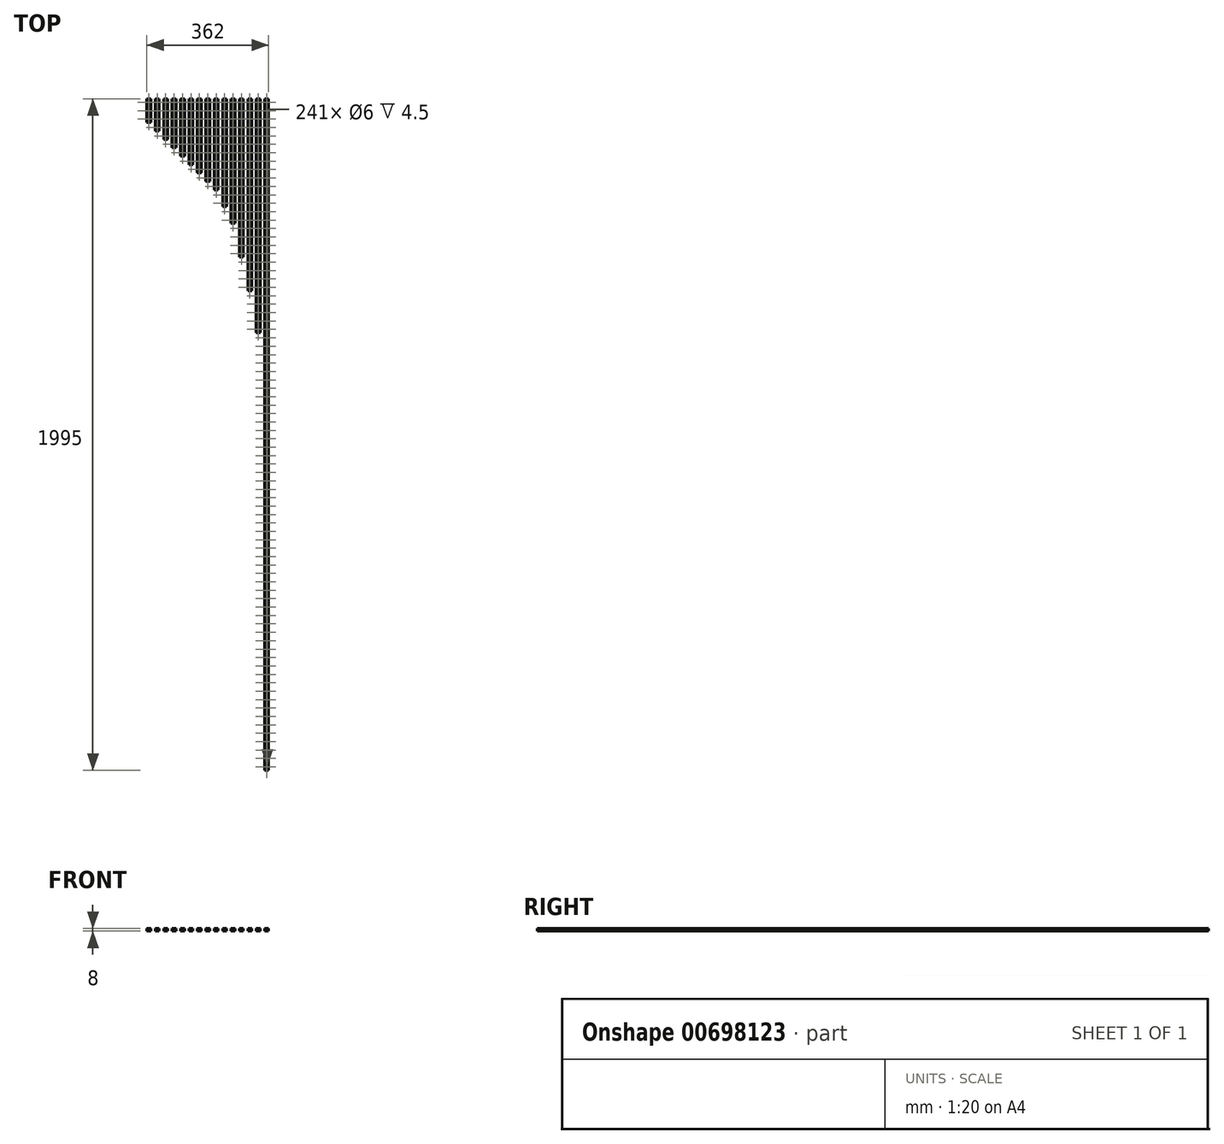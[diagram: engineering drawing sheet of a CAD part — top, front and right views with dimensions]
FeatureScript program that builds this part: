
annotation { "Feature Type Name" : "Feature", "Feature Type Description" : "" }
export const myFeature = defineFeature(function(context is Context, id is Id, definition is map)
    precondition{}
    {
        {
            var Q0;
            Q0=qCreatedBy(makeId("Front.planeOp"),FACE);
            var sketch = newSketch(context, id + "F0", { "sketchPlane" : qUnion([Q0])});
            skPoint(sketch, "E0.middle", {"position": v(0, 0) * mm});
            skLineSegment(sketch, "E1.bottom", {"start": v(5.5, -4) * mm, "end": v(-5.5, -4) * mm});
            skLineSegment(sketch, "E1.top", {"start": v(5.5, 4) * mm, "end": v(-5.5, 4) * mm});
            skLineSegment(sketch, "E1.left", {"start": v(6, -3.5) * mm, "end": v(6, -0.03) * mm});
            skLineSegment(sketch, "E1.right", {"start": v(-6, -3.5) * mm, "end": v(-6, -0.03) * mm});
            skArc(sketch, "E2", {"start": v(-6, -0.03) * mm, "mid": v(-5.5, 0.27) * mm, "end": v(-5.15, 0.75) * mm});
            skArc(sketch, "E3", {"start": v(6, 2.63) * mm, "mid": v(5.5, 2.33) * mm, "end": v(5.15, 1.85) * mm});
            skLineSegment(sketch, "E4", {"start": v(4.45, 1.85) * mm, "end": v(5.15, 1.85) * mm});
            skLineSegment(sketch, "E5", {"start": v(4.45, 0.75) * mm, "end": v(5.15, 0.75) * mm});
            skLineSegment(sketch, "E6", {"start": v(-4.45, 0.75) * mm, "end": v(-5.15, 0.75) * mm});
            skLineSegment(sketch, "E7", {"start": v(-4.45, 1.85) * mm, "end": v(-5.15, 1.85) * mm});
            skLineSegment(sketch, "E8", {"start": v(-6, 3.5) * mm, "end": v(-5.5, 4) * mm});
            skLineSegment(sketch, "E9.MirrorCS", {"start": v(6, 3.5) * mm, "end": v(5.5, 4) * mm});
            skLineSegment(sketch, "E10.MirrorCS", {"start": v(6, -3.5) * mm, "end": v(5.5, -4) * mm});
            skLineSegment(sketch, "E11.MirrorCS", {"start": v(-6, -3.5) * mm, "end": v(-5.5, -4) * mm});
            skPoint(sketch, "E12.orphan", {"position": v(-6, 4) * mm});
            skLineSegment(sketch, "E13.trimOffspring", {"start": v(-6, 2.63) * mm, "end": v(-6, 3.5) * mm});
            skArc(sketch, "E14.trimOffspring", {"start": v(-5.15, 1.85) * mm, "mid": v(-5.5, 2.33) * mm, "end": v(-6, 2.63) * mm});
            skPoint(sketch, "E15.orphan", {"position": v(6, 4) * mm});
            skLineSegment(sketch, "E16.trimOffspring", {"start": v(6, 2.63) * mm, "end": v(6, 3.5) * mm});
            skArc(sketch, "E17.trimOffspring", {"start": v(5.15, 0.75) * mm, "mid": v(5.5, 0.27) * mm, "end": v(6, -0.03) * mm});
            skPoint(sketch, "E18.orphan", {"position": v(6, -4) * mm});
            skPoint(sketch, "E19.orphan", {"position": v(-6, -4) * mm});
            skLineSegment(sketch, "E20", {"start": v(-4.45, 1.85) * mm, "end": v(-4.45, 0.75) * mm});
            skLineSegment(sketch, "E21", {"start": v(4.45, 1.85) * mm, "end": v(4.45, 0.75) * mm});
            skLineSegment(sketch, "E22", {"start": v(-6.44, 1.3) * mm, "end": v(6.44, 1.3) * mm, "construction": true});
            skLineSegment(sketch, "E23.1.0.0", {"start": v(18.56, 1.3) * mm, "end": v(31.44, 1.3) * mm, "construction": true});
            skLineSegment(sketch, "E23.1.0.1", {"start": v(19, -3.5) * mm, "end": v(19, -0.03) * mm});
            skLineSegment(sketch, "E23.1.0.2", {"start": v(31, -3.5) * mm, "end": v(31, -0.03) * mm});
            skLineSegment(sketch, "E23.1.0.3", {"start": v(30.5, -4) * mm, "end": v(19.5, -4) * mm});
            skLineSegment(sketch, "E23.1.0.4", {"start": v(30.5, 4) * mm, "end": v(19.5, 4) * mm});
            skPoint(sketch, "E23.1.0.5", {"position": v(25, 0) * mm});
            skPoint(sketch, "E23.1.0.6", {"position": v(19, -4) * mm});
            skPoint(sketch, "E23.1.0.7", {"position": v(19, 4) * mm});
            skPoint(sketch, "E23.1.0.8", {"position": v(31, 4) * mm});
            skPoint(sketch, "E23.1.0.9", {"position": v(31, -4) * mm});
            skPoint(sketch, "E23.1.0.10", {"position": v(25, 0) * mm});
            skLineSegment(sketch, "E23.1.0.11", {"start": v(31, -3.5) * mm, "end": v(30.5, -4) * mm});
            skLineSegment(sketch, "E23.1.0.12", {"start": v(31, 3.5) * mm, "end": v(30.5, 4) * mm});
            skLineSegment(sketch, "E23.1.0.13", {"start": v(19, -3.5) * mm, "end": v(19.5, -4) * mm});
            skLineSegment(sketch, "E23.1.0.14", {"start": v(20.55, 1.85) * mm, "end": v(19.85, 1.85) * mm});
            skLineSegment(sketch, "E23.1.0.15", {"start": v(19, 2.63) * mm, "end": v(19, 3.5) * mm});
            skLineSegment(sketch, "E23.1.0.16", {"start": v(31, 2.63) * mm, "end": v(31, 3.5) * mm});
            skArc(sketch, "E23.1.0.17", {"start": v(30.15, 0.75) * mm, "mid": v(30.5, 0.27) * mm, "end": v(31, -0.03) * mm});
            skLineSegment(sketch, "E23.1.0.18", {"start": v(20.55, 1.85) * mm, "end": v(20.55, 0.75) * mm});
            skLineSegment(sketch, "E23.1.0.19", {"start": v(29.45, 0.75) * mm, "end": v(30.15, 0.75) * mm});
            skLineSegment(sketch, "E23.1.0.20", {"start": v(20.55, 0.75) * mm, "end": v(19.85, 0.75) * mm});
            skArc(sketch, "E23.1.0.21", {"start": v(19, -0.03) * mm, "mid": v(19.5, 0.27) * mm, "end": v(19.85, 0.75) * mm});
            skLineSegment(sketch, "E23.1.0.22", {"start": v(19, 3.5) * mm, "end": v(19.5, 4) * mm});
            skArc(sketch, "E23.1.0.23", {"start": v(19.85, 1.85) * mm, "mid": v(19.5, 2.33) * mm, "end": v(19, 2.63) * mm});
            skLineSegment(sketch, "E23.1.0.24", {"start": v(29.45, 1.85) * mm, "end": v(30.15, 1.85) * mm});
            skArc(sketch, "E23.1.0.25", {"start": v(31, 2.63) * mm, "mid": v(30.5, 2.33) * mm, "end": v(30.15, 1.85) * mm});
            skArc(sketch, "E23.1.0.26", {"start": v(30.15, 0.75) * mm, "mid": v(30.5, 0.27) * mm, "end": v(31, -0.03) * mm});
            skLineSegment(sketch, "E23.1.0.27", {"start": v(29.45, 1.85) * mm, "end": v(29.45, 0.75) * mm});
            skLineSegment(sketch, "E23.2.0.0", {"start": v(43.56, 1.3) * mm, "end": v(56.44, 1.3) * mm, "construction": true});
            skLineSegment(sketch, "E23.2.0.1", {"start": v(44, -3.5) * mm, "end": v(44, -0.03) * mm});
            skLineSegment(sketch, "E23.2.0.2", {"start": v(56, -3.5) * mm, "end": v(56, -0.03) * mm});
            skLineSegment(sketch, "E23.2.0.3", {"start": v(55.5, -4) * mm, "end": v(44.5, -4) * mm});
            skLineSegment(sketch, "E23.2.0.4", {"start": v(55.5, 4) * mm, "end": v(44.5, 4) * mm});
            skPoint(sketch, "E23.2.0.5", {"position": v(50, 0) * mm});
            skPoint(sketch, "E23.2.0.6", {"position": v(44, -4) * mm});
            skPoint(sketch, "E23.2.0.7", {"position": v(44, 4) * mm});
            skPoint(sketch, "E23.2.0.8", {"position": v(56, 4) * mm});
            skPoint(sketch, "E23.2.0.9", {"position": v(56, -4) * mm});
            skPoint(sketch, "E23.2.0.10", {"position": v(50, 0) * mm});
            skLineSegment(sketch, "E23.2.0.11", {"start": v(56, -3.5) * mm, "end": v(55.5, -4) * mm});
            skLineSegment(sketch, "E23.2.0.12", {"start": v(56, 3.5) * mm, "end": v(55.5, 4) * mm});
            skLineSegment(sketch, "E23.2.0.13", {"start": v(44, -3.5) * mm, "end": v(44.5, -4) * mm});
            skLineSegment(sketch, "E23.2.0.14", {"start": v(45.55, 1.85) * mm, "end": v(44.85, 1.85) * mm});
            skLineSegment(sketch, "E23.2.0.15", {"start": v(44, 2.63) * mm, "end": v(44, 3.5) * mm});
            skLineSegment(sketch, "E23.2.0.16", {"start": v(56, 2.63) * mm, "end": v(56, 3.5) * mm});
            skArc(sketch, "E23.2.0.17", {"start": v(55.15, 0.75) * mm, "mid": v(55.5, 0.27) * mm, "end": v(56, -0.03) * mm});
            skLineSegment(sketch, "E23.2.0.18", {"start": v(45.55, 1.85) * mm, "end": v(45.55, 0.75) * mm});
            skLineSegment(sketch, "E23.2.0.19", {"start": v(54.45, 0.75) * mm, "end": v(55.15, 0.75) * mm});
            skLineSegment(sketch, "E23.2.0.20", {"start": v(45.55, 0.75) * mm, "end": v(44.85, 0.75) * mm});
            skArc(sketch, "E23.2.0.21", {"start": v(44, -0.03) * mm, "mid": v(44.5, 0.27) * mm, "end": v(44.85, 0.75) * mm});
            skLineSegment(sketch, "E23.2.0.22", {"start": v(44, 3.5) * mm, "end": v(44.5, 4) * mm});
            skArc(sketch, "E23.2.0.23", {"start": v(44.85, 1.85) * mm, "mid": v(44.5, 2.33) * mm, "end": v(44, 2.63) * mm});
            skLineSegment(sketch, "E23.2.0.24", {"start": v(54.45, 1.85) * mm, "end": v(55.15, 1.85) * mm});
            skArc(sketch, "E23.2.0.25", {"start": v(56, 2.63) * mm, "mid": v(55.5, 2.33) * mm, "end": v(55.15, 1.85) * mm});
            skArc(sketch, "E23.2.0.26", {"start": v(55.15, 0.75) * mm, "mid": v(55.5, 0.27) * mm, "end": v(56, -0.03) * mm});
            skLineSegment(sketch, "E23.2.0.27", {"start": v(54.45, 1.85) * mm, "end": v(54.45, 0.75) * mm});
            skLineSegment(sketch, "E23.3.0.0", {"start": v(68.56, 1.3) * mm, "end": v(81.44, 1.3) * mm, "construction": true});
            skLineSegment(sketch, "E23.3.0.1", {"start": v(69, -3.5) * mm, "end": v(69, -0.03) * mm});
            skLineSegment(sketch, "E23.3.0.2", {"start": v(81, -3.5) * mm, "end": v(81, -0.03) * mm});
            skLineSegment(sketch, "E23.3.0.3", {"start": v(80.5, -4) * mm, "end": v(69.5, -4) * mm});
            skLineSegment(sketch, "E23.3.0.4", {"start": v(80.5, 4) * mm, "end": v(69.5, 4) * mm});
            skPoint(sketch, "E23.3.0.5", {"position": v(75, 0) * mm});
            skPoint(sketch, "E23.3.0.6", {"position": v(69, -4) * mm});
            skPoint(sketch, "E23.3.0.7", {"position": v(69, 4) * mm});
            skPoint(sketch, "E23.3.0.8", {"position": v(81, 4) * mm});
            skPoint(sketch, "E23.3.0.9", {"position": v(81, -4) * mm});
            skPoint(sketch, "E23.3.0.10", {"position": v(75, 0) * mm});
            skLineSegment(sketch, "E23.3.0.11", {"start": v(81, -3.5) * mm, "end": v(80.5, -4) * mm});
            skLineSegment(sketch, "E23.3.0.12", {"start": v(81, 3.5) * mm, "end": v(80.5, 4) * mm});
            skLineSegment(sketch, "E23.3.0.13", {"start": v(69, -3.5) * mm, "end": v(69.5, -4) * mm});
            skLineSegment(sketch, "E23.3.0.14", {"start": v(70.55, 1.85) * mm, "end": v(69.85, 1.85) * mm});
            skLineSegment(sketch, "E23.3.0.15", {"start": v(69, 2.63) * mm, "end": v(69, 3.5) * mm});
            skLineSegment(sketch, "E23.3.0.16", {"start": v(81, 2.63) * mm, "end": v(81, 3.5) * mm});
            skArc(sketch, "E23.3.0.17", {"start": v(80.15, 0.75) * mm, "mid": v(80.5, 0.27) * mm, "end": v(81, -0.03) * mm});
            skLineSegment(sketch, "E23.3.0.18", {"start": v(70.55, 1.85) * mm, "end": v(70.55, 0.75) * mm});
            skLineSegment(sketch, "E23.3.0.19", {"start": v(79.45, 0.75) * mm, "end": v(80.15, 0.75) * mm});
            skLineSegment(sketch, "E23.3.0.20", {"start": v(70.55, 0.75) * mm, "end": v(69.85, 0.75) * mm});
            skArc(sketch, "E23.3.0.21", {"start": v(69, -0.03) * mm, "mid": v(69.5, 0.27) * mm, "end": v(69.85, 0.75) * mm});
            skLineSegment(sketch, "E23.3.0.22", {"start": v(69, 3.5) * mm, "end": v(69.5, 4) * mm});
            skArc(sketch, "E23.3.0.23", {"start": v(69.85, 1.85) * mm, "mid": v(69.5, 2.33) * mm, "end": v(69, 2.63) * mm});
            skLineSegment(sketch, "E23.3.0.24", {"start": v(79.45, 1.85) * mm, "end": v(80.15, 1.85) * mm});
            skArc(sketch, "E23.3.0.25", {"start": v(81, 2.63) * mm, "mid": v(80.5, 2.33) * mm, "end": v(80.15, 1.85) * mm});
            skArc(sketch, "E23.3.0.26", {"start": v(80.15, 0.75) * mm, "mid": v(80.5, 0.27) * mm, "end": v(81, -0.03) * mm});
            skLineSegment(sketch, "E23.3.0.27", {"start": v(79.45, 1.85) * mm, "end": v(79.45, 0.75) * mm});
            skLineSegment(sketch, "E23.4.0.0", {"start": v(93.56, 1.3) * mm, "end": v(106.44, 1.3) * mm, "construction": true});
            skLineSegment(sketch, "E23.4.0.1", {"start": v(94, -3.5) * mm, "end": v(94, -0.03) * mm});
            skLineSegment(sketch, "E23.4.0.2", {"start": v(106, -3.5) * mm, "end": v(106, -0.03) * mm});
            skLineSegment(sketch, "E23.4.0.3", {"start": v(105.5, -4) * mm, "end": v(94.5, -4) * mm});
            skLineSegment(sketch, "E23.4.0.4", {"start": v(105.5, 4) * mm, "end": v(94.5, 4) * mm});
            skPoint(sketch, "E23.4.0.5", {"position": v(100, 0) * mm});
            skPoint(sketch, "E23.4.0.6", {"position": v(94, -4) * mm});
            skPoint(sketch, "E23.4.0.7", {"position": v(94, 4) * mm});
            skPoint(sketch, "E23.4.0.8", {"position": v(106, 4) * mm});
            skPoint(sketch, "E23.4.0.9", {"position": v(106, -4) * mm});
            skPoint(sketch, "E23.4.0.10", {"position": v(100, 0) * mm});
            skLineSegment(sketch, "E23.4.0.11", {"start": v(106, -3.5) * mm, "end": v(105.5, -4) * mm});
            skLineSegment(sketch, "E23.4.0.12", {"start": v(106, 3.5) * mm, "end": v(105.5, 4) * mm});
            skLineSegment(sketch, "E23.4.0.13", {"start": v(94, -3.5) * mm, "end": v(94.5, -4) * mm});
            skLineSegment(sketch, "E23.4.0.14", {"start": v(95.55, 1.85) * mm, "end": v(94.85, 1.85) * mm});
            skLineSegment(sketch, "E23.4.0.15", {"start": v(94, 2.63) * mm, "end": v(94, 3.5) * mm});
            skLineSegment(sketch, "E23.4.0.16", {"start": v(106, 2.63) * mm, "end": v(106, 3.5) * mm});
            skArc(sketch, "E23.4.0.17", {"start": v(105.15, 0.75) * mm, "mid": v(105.5, 0.27) * mm, "end": v(106, -0.03) * mm});
            skLineSegment(sketch, "E23.4.0.18", {"start": v(95.55, 1.85) * mm, "end": v(95.55, 0.75) * mm});
            skLineSegment(sketch, "E23.4.0.19", {"start": v(104.45, 0.75) * mm, "end": v(105.15, 0.75) * mm});
            skLineSegment(sketch, "E23.4.0.20", {"start": v(95.55, 0.75) * mm, "end": v(94.85, 0.75) * mm});
            skArc(sketch, "E23.4.0.21", {"start": v(94, -0.03) * mm, "mid": v(94.5, 0.27) * mm, "end": v(94.85, 0.75) * mm});
            skLineSegment(sketch, "E23.4.0.22", {"start": v(94, 3.5) * mm, "end": v(94.5, 4) * mm});
            skArc(sketch, "E23.4.0.23", {"start": v(94.85, 1.85) * mm, "mid": v(94.5, 2.33) * mm, "end": v(94, 2.63) * mm});
            skLineSegment(sketch, "E23.4.0.24", {"start": v(104.45, 1.85) * mm, "end": v(105.15, 1.85) * mm});
            skArc(sketch, "E23.4.0.25", {"start": v(106, 2.63) * mm, "mid": v(105.5, 2.33) * mm, "end": v(105.15, 1.85) * mm});
            skArc(sketch, "E23.4.0.26", {"start": v(105.15, 0.75) * mm, "mid": v(105.5, 0.27) * mm, "end": v(106, -0.03) * mm});
            skLineSegment(sketch, "E23.4.0.27", {"start": v(104.45, 1.85) * mm, "end": v(104.45, 0.75) * mm});
            skLineSegment(sketch, "E23.5.0.0", {"start": v(118.56, 1.3) * mm, "end": v(131.44, 1.3) * mm, "construction": true});
            skLineSegment(sketch, "E23.5.0.1", {"start": v(119, -3.5) * mm, "end": v(119, -0.03) * mm});
            skLineSegment(sketch, "E23.5.0.2", {"start": v(131, -3.5) * mm, "end": v(131, -0.03) * mm});
            skLineSegment(sketch, "E23.5.0.3", {"start": v(130.5, -4) * mm, "end": v(119.5, -4) * mm});
            skLineSegment(sketch, "E23.5.0.4", {"start": v(130.5, 4) * mm, "end": v(119.5, 4) * mm});
            skPoint(sketch, "E23.5.0.5", {"position": v(125, 0) * mm});
            skPoint(sketch, "E23.5.0.6", {"position": v(119, -4) * mm});
            skPoint(sketch, "E23.5.0.7", {"position": v(119, 4) * mm});
            skPoint(sketch, "E23.5.0.8", {"position": v(131, 4) * mm});
            skPoint(sketch, "E23.5.0.9", {"position": v(131, -4) * mm});
            skPoint(sketch, "E23.5.0.10", {"position": v(125, 0) * mm});
            skLineSegment(sketch, "E23.5.0.11", {"start": v(131, -3.5) * mm, "end": v(130.5, -4) * mm});
            skLineSegment(sketch, "E23.5.0.12", {"start": v(131, 3.5) * mm, "end": v(130.5, 4) * mm});
            skLineSegment(sketch, "E23.5.0.13", {"start": v(119, -3.5) * mm, "end": v(119.5, -4) * mm});
            skLineSegment(sketch, "E23.5.0.14", {"start": v(120.55, 1.85) * mm, "end": v(119.85, 1.85) * mm});
            skLineSegment(sketch, "E23.5.0.15", {"start": v(119, 2.63) * mm, "end": v(119, 3.5) * mm});
            skLineSegment(sketch, "E23.5.0.16", {"start": v(131, 2.63) * mm, "end": v(131, 3.5) * mm});
            skArc(sketch, "E23.5.0.17", {"start": v(130.15, 0.75) * mm, "mid": v(130.5, 0.27) * mm, "end": v(131, -0.03) * mm});
            skLineSegment(sketch, "E23.5.0.18", {"start": v(120.55, 1.85) * mm, "end": v(120.55, 0.75) * mm});
            skLineSegment(sketch, "E23.5.0.19", {"start": v(129.45, 0.75) * mm, "end": v(130.15, 0.75) * mm});
            skLineSegment(sketch, "E23.5.0.20", {"start": v(120.55, 0.75) * mm, "end": v(119.85, 0.75) * mm});
            skArc(sketch, "E23.5.0.21", {"start": v(119, -0.03) * mm, "mid": v(119.5, 0.27) * mm, "end": v(119.85, 0.75) * mm});
            skLineSegment(sketch, "E23.5.0.22", {"start": v(119, 3.5) * mm, "end": v(119.5, 4) * mm});
            skArc(sketch, "E23.5.0.23", {"start": v(119.85, 1.85) * mm, "mid": v(119.5, 2.33) * mm, "end": v(119, 2.63) * mm});
            skLineSegment(sketch, "E23.5.0.24", {"start": v(129.45, 1.85) * mm, "end": v(130.15, 1.85) * mm});
            skArc(sketch, "E23.5.0.25", {"start": v(131, 2.63) * mm, "mid": v(130.5, 2.33) * mm, "end": v(130.15, 1.85) * mm});
            skArc(sketch, "E23.5.0.26", {"start": v(130.15, 0.75) * mm, "mid": v(130.5, 0.27) * mm, "end": v(131, -0.03) * mm});
            skLineSegment(sketch, "E23.5.0.27", {"start": v(129.45, 1.85) * mm, "end": v(129.45, 0.75) * mm});
            skLineSegment(sketch, "E23.6.0.0", {"start": v(143.56, 1.3) * mm, "end": v(156.44, 1.3) * mm, "construction": true});
            skLineSegment(sketch, "E23.6.0.1", {"start": v(144, -3.5) * mm, "end": v(144, -0.03) * mm});
            skLineSegment(sketch, "E23.6.0.2", {"start": v(156, -3.5) * mm, "end": v(156, -0.03) * mm});
            skLineSegment(sketch, "E23.6.0.3", {"start": v(155.5, -4) * mm, "end": v(144.5, -4) * mm});
            skLineSegment(sketch, "E23.6.0.4", {"start": v(155.5, 4) * mm, "end": v(144.5, 4) * mm});
            skPoint(sketch, "E23.6.0.5", {"position": v(150, 0) * mm});
            skPoint(sketch, "E23.6.0.6", {"position": v(144, -4) * mm});
            skPoint(sketch, "E23.6.0.7", {"position": v(144, 4) * mm});
            skPoint(sketch, "E23.6.0.8", {"position": v(156, 4) * mm});
            skPoint(sketch, "E23.6.0.9", {"position": v(156, -4) * mm});
            skPoint(sketch, "E23.6.0.10", {"position": v(150, 0) * mm});
            skLineSegment(sketch, "E23.6.0.11", {"start": v(156, -3.5) * mm, "end": v(155.5, -4) * mm});
            skLineSegment(sketch, "E23.6.0.12", {"start": v(156, 3.5) * mm, "end": v(155.5, 4) * mm});
            skLineSegment(sketch, "E23.6.0.13", {"start": v(144, -3.5) * mm, "end": v(144.5, -4) * mm});
            skLineSegment(sketch, "E23.6.0.14", {"start": v(145.55, 1.85) * mm, "end": v(144.85, 1.85) * mm});
            skLineSegment(sketch, "E23.6.0.15", {"start": v(144, 2.63) * mm, "end": v(144, 3.5) * mm});
            skLineSegment(sketch, "E23.6.0.16", {"start": v(156, 2.63) * mm, "end": v(156, 3.5) * mm});
            skArc(sketch, "E23.6.0.17", {"start": v(155.15, 0.75) * mm, "mid": v(155.5, 0.27) * mm, "end": v(156, -0.03) * mm});
            skLineSegment(sketch, "E23.6.0.18", {"start": v(145.55, 1.85) * mm, "end": v(145.55, 0.75) * mm});
            skLineSegment(sketch, "E23.6.0.19", {"start": v(154.45, 0.75) * mm, "end": v(155.15, 0.75) * mm});
            skLineSegment(sketch, "E23.6.0.20", {"start": v(145.55, 0.75) * mm, "end": v(144.85, 0.75) * mm});
            skArc(sketch, "E23.6.0.21", {"start": v(144, -0.03) * mm, "mid": v(144.5, 0.27) * mm, "end": v(144.85, 0.75) * mm});
            skLineSegment(sketch, "E23.6.0.22", {"start": v(144, 3.5) * mm, "end": v(144.5, 4) * mm});
            skArc(sketch, "E23.6.0.23", {"start": v(144.85, 1.85) * mm, "mid": v(144.5, 2.33) * mm, "end": v(144, 2.63) * mm});
            skLineSegment(sketch, "E23.6.0.24", {"start": v(154.45, 1.85) * mm, "end": v(155.15, 1.85) * mm});
            skArc(sketch, "E23.6.0.25", {"start": v(156, 2.63) * mm, "mid": v(155.5, 2.33) * mm, "end": v(155.15, 1.85) * mm});
            skArc(sketch, "E23.6.0.26", {"start": v(155.15, 0.75) * mm, "mid": v(155.5, 0.27) * mm, "end": v(156, -0.03) * mm});
            skLineSegment(sketch, "E23.6.0.27", {"start": v(154.45, 1.85) * mm, "end": v(154.45, 0.75) * mm});
            skLineSegment(sketch, "E23.direction1", {"start": v(-6, -4) * mm, "end": v(19, -4) * mm, "construction": true});
            skLineSegment(sketch, "E24.0.7.0", {"start": v(168.56, 1.3) * mm, "end": v(181.44, 1.3) * mm, "construction": true});
            skLineSegment(sketch, "E24.3.7.0", {"start": v(169, -3.5) * mm, "end": v(169, -0.03) * mm});
            skLineSegment(sketch, "E24.6.7.0", {"start": v(181, -3.5) * mm, "end": v(181, -0.03) * mm});
            skLineSegment(sketch, "E24.9.7.0", {"start": v(180.5, -4) * mm, "end": v(169.5, -4) * mm});
            skLineSegment(sketch, "E24.12.7.0", {"start": v(180.5, 4) * mm, "end": v(169.5, 4) * mm});
            skPoint(sketch, "E24.15.7.0", {"position": v(175, 0) * mm});
            skPoint(sketch, "E24.16.7.0", {"position": v(169, -4) * mm});
            skPoint(sketch, "E24.17.7.0", {"position": v(169, 4) * mm});
            skPoint(sketch, "E24.18.7.0", {"position": v(181, 4) * mm});
            skPoint(sketch, "E24.19.7.0", {"position": v(181, -4) * mm});
            skPoint(sketch, "E24.20.7.0", {"position": v(175, 0) * mm});
            skLineSegment(sketch, "E24.21.7.0", {"start": v(181, -3.5) * mm, "end": v(180.5, -4) * mm});
            skLineSegment(sketch, "E24.24.7.0", {"start": v(181, 3.5) * mm, "end": v(180.5, 4) * mm});
            skLineSegment(sketch, "E24.27.7.0", {"start": v(169, -3.5) * mm, "end": v(169.5, -4) * mm});
            skLineSegment(sketch, "E24.30.7.0", {"start": v(170.55, 1.85) * mm, "end": v(169.85, 1.85) * mm});
            skLineSegment(sketch, "E24.33.7.0", {"start": v(169, 2.63) * mm, "end": v(169, 3.5) * mm});
            skLineSegment(sketch, "E24.36.7.0", {"start": v(181, 2.63) * mm, "end": v(181, 3.5) * mm});
            skArc(sketch, "E24.39.7.0", {"start": v(180.15, 0.75) * mm, "mid": v(180.5, 0.27) * mm, "end": v(181, -0.03) * mm});
            skLineSegment(sketch, "E24.43.7.0", {"start": v(170.55, 1.85) * mm, "end": v(170.55, 0.75) * mm});
            skLineSegment(sketch, "E24.46.7.0", {"start": v(179.45, 0.75) * mm, "end": v(180.15, 0.75) * mm});
            skLineSegment(sketch, "E24.49.7.0", {"start": v(170.55, 0.75) * mm, "end": v(169.85, 0.75) * mm});
            skArc(sketch, "E24.52.7.0", {"start": v(169, -0.03) * mm, "mid": v(169.5, 0.27) * mm, "end": v(169.85, 0.75) * mm});
            skLineSegment(sketch, "E24.56.7.0", {"start": v(169, 3.5) * mm, "end": v(169.5, 4) * mm});
            skArc(sketch, "E24.59.7.0", {"start": v(169.85, 1.85) * mm, "mid": v(169.5, 2.33) * mm, "end": v(169, 2.63) * mm});
            skLineSegment(sketch, "E24.63.7.0", {"start": v(179.45, 1.85) * mm, "end": v(180.15, 1.85) * mm});
            skArc(sketch, "E24.66.7.0", {"start": v(181, 2.63) * mm, "mid": v(180.5, 2.33) * mm, "end": v(180.15, 1.85) * mm});
            skArc(sketch, "E24.70.7.0", {"start": v(180.15, 0.75) * mm, "mid": v(180.5, 0.27) * mm, "end": v(181, -0.03) * mm});
            skLineSegment(sketch, "E24.74.7.0", {"start": v(179.45, 1.85) * mm, "end": v(179.45, 0.75) * mm});
            skLineSegment(sketch, "E24.0.8.0", {"start": v(193.56, 1.3) * mm, "end": v(206.44, 1.3) * mm, "construction": true});
            skLineSegment(sketch, "E24.3.8.0", {"start": v(194, -3.5) * mm, "end": v(194, -0.03) * mm});
            skLineSegment(sketch, "E24.6.8.0", {"start": v(206, -3.5) * mm, "end": v(206, -0.03) * mm});
            skLineSegment(sketch, "E24.9.8.0", {"start": v(205.5, -4) * mm, "end": v(194.5, -4) * mm});
            skLineSegment(sketch, "E24.12.8.0", {"start": v(205.5, 4) * mm, "end": v(194.5, 4) * mm});
            skPoint(sketch, "E24.15.8.0", {"position": v(200, 0) * mm});
            skPoint(sketch, "E24.16.8.0", {"position": v(194, -4) * mm});
            skPoint(sketch, "E24.17.8.0", {"position": v(194, 4) * mm});
            skPoint(sketch, "E24.18.8.0", {"position": v(206, 4) * mm});
            skPoint(sketch, "E24.19.8.0", {"position": v(206, -4) * mm});
            skPoint(sketch, "E24.20.8.0", {"position": v(200, 0) * mm});
            skLineSegment(sketch, "E24.21.8.0", {"start": v(206, -3.5) * mm, "end": v(205.5, -4) * mm});
            skLineSegment(sketch, "E24.24.8.0", {"start": v(206, 3.5) * mm, "end": v(205.5, 4) * mm});
            skLineSegment(sketch, "E24.27.8.0", {"start": v(194, -3.5) * mm, "end": v(194.5, -4) * mm});
            skLineSegment(sketch, "E24.30.8.0", {"start": v(195.55, 1.85) * mm, "end": v(194.85, 1.85) * mm});
            skLineSegment(sketch, "E24.33.8.0", {"start": v(194, 2.63) * mm, "end": v(194, 3.5) * mm});
            skLineSegment(sketch, "E24.36.8.0", {"start": v(206, 2.63) * mm, "end": v(206, 3.5) * mm});
            skArc(sketch, "E24.39.8.0", {"start": v(205.15, 0.75) * mm, "mid": v(205.5, 0.27) * mm, "end": v(206, -0.03) * mm});
            skLineSegment(sketch, "E24.43.8.0", {"start": v(195.55, 1.85) * mm, "end": v(195.55, 0.75) * mm});
            skLineSegment(sketch, "E24.46.8.0", {"start": v(204.45, 0.75) * mm, "end": v(205.15, 0.75) * mm});
            skLineSegment(sketch, "E24.49.8.0", {"start": v(195.55, 0.75) * mm, "end": v(194.85, 0.75) * mm});
            skArc(sketch, "E24.52.8.0", {"start": v(194, -0.03) * mm, "mid": v(194.5, 0.27) * mm, "end": v(194.85, 0.75) * mm});
            skLineSegment(sketch, "E24.56.8.0", {"start": v(194, 3.5) * mm, "end": v(194.5, 4) * mm});
            skArc(sketch, "E24.59.8.0", {"start": v(194.85, 1.85) * mm, "mid": v(194.5, 2.33) * mm, "end": v(194, 2.63) * mm});
            skLineSegment(sketch, "E24.63.8.0", {"start": v(204.45, 1.85) * mm, "end": v(205.15, 1.85) * mm});
            skArc(sketch, "E24.66.8.0", {"start": v(206, 2.63) * mm, "mid": v(205.5, 2.33) * mm, "end": v(205.15, 1.85) * mm});
            skArc(sketch, "E24.70.8.0", {"start": v(205.15, 0.75) * mm, "mid": v(205.5, 0.27) * mm, "end": v(206, -0.03) * mm});
            skLineSegment(sketch, "E24.74.8.0", {"start": v(204.45, 1.85) * mm, "end": v(204.45, 0.75) * mm});
            skLineSegment(sketch, "E24.0.9.0", {"start": v(218.56, 1.3) * mm, "end": v(231.44, 1.3) * mm, "construction": true});
            skLineSegment(sketch, "E24.3.9.0", {"start": v(219, -3.5) * mm, "end": v(219, -0.03) * mm});
            skLineSegment(sketch, "E24.6.9.0", {"start": v(231, -3.5) * mm, "end": v(231, -0.03) * mm});
            skLineSegment(sketch, "E24.9.9.0", {"start": v(230.5, -4) * mm, "end": v(219.5, -4) * mm});
            skLineSegment(sketch, "E24.12.9.0", {"start": v(230.5, 4) * mm, "end": v(219.5, 4) * mm});
            skPoint(sketch, "E24.15.9.0", {"position": v(225, 0) * mm});
            skPoint(sketch, "E24.16.9.0", {"position": v(219, -4) * mm});
            skPoint(sketch, "E24.17.9.0", {"position": v(219, 4) * mm});
            skPoint(sketch, "E24.18.9.0", {"position": v(231, 4) * mm});
            skPoint(sketch, "E24.19.9.0", {"position": v(231, -4) * mm});
            skPoint(sketch, "E24.20.9.0", {"position": v(225, 0) * mm});
            skLineSegment(sketch, "E24.21.9.0", {"start": v(231, -3.5) * mm, "end": v(230.5, -4) * mm});
            skLineSegment(sketch, "E24.24.9.0", {"start": v(231, 3.5) * mm, "end": v(230.5, 4) * mm});
            skLineSegment(sketch, "E24.27.9.0", {"start": v(219, -3.5) * mm, "end": v(219.5, -4) * mm});
            skLineSegment(sketch, "E24.30.9.0", {"start": v(220.55, 1.85) * mm, "end": v(219.85, 1.85) * mm});
            skLineSegment(sketch, "E24.33.9.0", {"start": v(219, 2.63) * mm, "end": v(219, 3.5) * mm});
            skLineSegment(sketch, "E24.36.9.0", {"start": v(231, 2.63) * mm, "end": v(231, 3.5) * mm});
            skArc(sketch, "E24.39.9.0", {"start": v(230.15, 0.75) * mm, "mid": v(230.5, 0.27) * mm, "end": v(231, -0.03) * mm});
            skLineSegment(sketch, "E24.43.9.0", {"start": v(220.55, 1.85) * mm, "end": v(220.55, 0.75) * mm});
            skLineSegment(sketch, "E24.46.9.0", {"start": v(229.45, 0.75) * mm, "end": v(230.15, 0.75) * mm});
            skLineSegment(sketch, "E24.49.9.0", {"start": v(220.55, 0.75) * mm, "end": v(219.85, 0.75) * mm});
            skArc(sketch, "E24.52.9.0", {"start": v(219, -0.03) * mm, "mid": v(219.5, 0.27) * mm, "end": v(219.85, 0.75) * mm});
            skLineSegment(sketch, "E24.56.9.0", {"start": v(219, 3.5) * mm, "end": v(219.5, 4) * mm});
            skArc(sketch, "E24.59.9.0", {"start": v(219.85, 1.85) * mm, "mid": v(219.5, 2.33) * mm, "end": v(219, 2.63) * mm});
            skLineSegment(sketch, "E24.63.9.0", {"start": v(229.45, 1.85) * mm, "end": v(230.15, 1.85) * mm});
            skArc(sketch, "E24.66.9.0", {"start": v(231, 2.63) * mm, "mid": v(230.5, 2.33) * mm, "end": v(230.15, 1.85) * mm});
            skArc(sketch, "E24.70.9.0", {"start": v(230.15, 0.75) * mm, "mid": v(230.5, 0.27) * mm, "end": v(231, -0.03) * mm});
            skLineSegment(sketch, "E24.74.9.0", {"start": v(229.45, 1.85) * mm, "end": v(229.45, 0.75) * mm});
            skLineSegment(sketch, "E24.0.10.0", {"start": v(243.56, 1.3) * mm, "end": v(256.44, 1.3) * mm, "construction": true});
            skLineSegment(sketch, "E24.3.10.0", {"start": v(244, -3.5) * mm, "end": v(244, -0.03) * mm});
            skLineSegment(sketch, "E24.6.10.0", {"start": v(256, -3.5) * mm, "end": v(256, -0.03) * mm});
            skLineSegment(sketch, "E24.9.10.0", {"start": v(255.5, -4) * mm, "end": v(244.5, -4) * mm});
            skLineSegment(sketch, "E24.12.10.0", {"start": v(255.5, 4) * mm, "end": v(244.5, 4) * mm});
            skPoint(sketch, "E24.15.10.0", {"position": v(250, 0) * mm});
            skPoint(sketch, "E24.16.10.0", {"position": v(244, -4) * mm});
            skPoint(sketch, "E24.17.10.0", {"position": v(244, 4) * mm});
            skPoint(sketch, "E24.18.10.0", {"position": v(256, 4) * mm});
            skPoint(sketch, "E24.19.10.0", {"position": v(256, -4) * mm});
            skPoint(sketch, "E24.20.10.0", {"position": v(250, 0) * mm});
            skLineSegment(sketch, "E24.21.10.0", {"start": v(256, -3.5) * mm, "end": v(255.5, -4) * mm});
            skLineSegment(sketch, "E24.24.10.0", {"start": v(256, 3.5) * mm, "end": v(255.5, 4) * mm});
            skLineSegment(sketch, "E24.27.10.0", {"start": v(244, -3.5) * mm, "end": v(244.5, -4) * mm});
            skLineSegment(sketch, "E24.30.10.0", {"start": v(245.55, 1.85) * mm, "end": v(244.85, 1.85) * mm});
            skLineSegment(sketch, "E24.33.10.0", {"start": v(244, 2.63) * mm, "end": v(244, 3.5) * mm});
            skLineSegment(sketch, "E24.36.10.0", {"start": v(256, 2.63) * mm, "end": v(256, 3.5) * mm});
            skArc(sketch, "E24.39.10.0", {"start": v(255.15, 0.75) * mm, "mid": v(255.5, 0.27) * mm, "end": v(256, -0.03) * mm});
            skLineSegment(sketch, "E24.43.10.0", {"start": v(245.55, 1.85) * mm, "end": v(245.55, 0.75) * mm});
            skLineSegment(sketch, "E24.46.10.0", {"start": v(254.45, 0.75) * mm, "end": v(255.15, 0.75) * mm});
            skLineSegment(sketch, "E24.49.10.0", {"start": v(245.55, 0.75) * mm, "end": v(244.85, 0.75) * mm});
            skArc(sketch, "E24.52.10.0", {"start": v(244, -0.03) * mm, "mid": v(244.5, 0.27) * mm, "end": v(244.85, 0.75) * mm});
            skLineSegment(sketch, "E24.56.10.0", {"start": v(244, 3.5) * mm, "end": v(244.5, 4) * mm});
            skArc(sketch, "E24.59.10.0", {"start": v(244.85, 1.85) * mm, "mid": v(244.5, 2.33) * mm, "end": v(244, 2.63) * mm});
            skLineSegment(sketch, "E24.63.10.0", {"start": v(254.45, 1.85) * mm, "end": v(255.15, 1.85) * mm});
            skArc(sketch, "E24.66.10.0", {"start": v(256, 2.63) * mm, "mid": v(255.5, 2.33) * mm, "end": v(255.15, 1.85) * mm});
            skArc(sketch, "E24.70.10.0", {"start": v(255.15, 0.75) * mm, "mid": v(255.5, 0.27) * mm, "end": v(256, -0.03) * mm});
            skLineSegment(sketch, "E24.74.10.0", {"start": v(254.45, 1.85) * mm, "end": v(254.45, 0.75) * mm});
            skLineSegment(sketch, "E25.0.11.0", {"start": v(268.56, 1.3) * mm, "end": v(281.44, 1.3) * mm, "construction": true});
            skLineSegment(sketch, "E25.3.11.0", {"start": v(269, -3.5) * mm, "end": v(269, -0.03) * mm});
            skLineSegment(sketch, "E25.6.11.0", {"start": v(281, -3.5) * mm, "end": v(281, -0.03) * mm});
            skLineSegment(sketch, "E25.9.11.0", {"start": v(280.5, -4) * mm, "end": v(269.5, -4) * mm});
            skLineSegment(sketch, "E25.12.11.0", {"start": v(280.5, 4) * mm, "end": v(269.5, 4) * mm});
            skPoint(sketch, "E25.15.11.0", {"position": v(275, 0) * mm});
            skPoint(sketch, "E25.16.11.0", {"position": v(269, -4) * mm});
            skPoint(sketch, "E25.17.11.0", {"position": v(269, 4) * mm});
            skPoint(sketch, "E25.18.11.0", {"position": v(281, 4) * mm});
            skPoint(sketch, "E25.19.11.0", {"position": v(281, -4) * mm});
            skPoint(sketch, "E25.20.11.0", {"position": v(275, 0) * mm});
            skLineSegment(sketch, "E25.21.11.0", {"start": v(281, -3.5) * mm, "end": v(280.5, -4) * mm});
            skLineSegment(sketch, "E25.24.11.0", {"start": v(281, 3.5) * mm, "end": v(280.5, 4) * mm});
            skLineSegment(sketch, "E25.27.11.0", {"start": v(269, -3.5) * mm, "end": v(269.5, -4) * mm});
            skLineSegment(sketch, "E25.30.11.0", {"start": v(270.55, 1.85) * mm, "end": v(269.85, 1.85) * mm});
            skLineSegment(sketch, "E25.33.11.0", {"start": v(269, 2.63) * mm, "end": v(269, 3.5) * mm});
            skLineSegment(sketch, "E25.36.11.0", {"start": v(281, 2.63) * mm, "end": v(281, 3.5) * mm});
            skArc(sketch, "E25.39.11.0", {"start": v(280.15, 0.75) * mm, "mid": v(280.5, 0.27) * mm, "end": v(281, -0.03) * mm});
            skLineSegment(sketch, "E25.43.11.0", {"start": v(270.55, 1.85) * mm, "end": v(270.55, 0.75) * mm});
            skLineSegment(sketch, "E25.46.11.0", {"start": v(279.45, 0.75) * mm, "end": v(280.15, 0.75) * mm});
            skLineSegment(sketch, "E25.49.11.0", {"start": v(270.55, 0.75) * mm, "end": v(269.85, 0.75) * mm});
            skArc(sketch, "E25.52.11.0", {"start": v(269, -0.03) * mm, "mid": v(269.5, 0.27) * mm, "end": v(269.85, 0.75) * mm});
            skLineSegment(sketch, "E25.56.11.0", {"start": v(269, 3.5) * mm, "end": v(269.5, 4) * mm});
            skArc(sketch, "E25.59.11.0", {"start": v(269.85, 1.85) * mm, "mid": v(269.5, 2.33) * mm, "end": v(269, 2.63) * mm});
            skLineSegment(sketch, "E25.63.11.0", {"start": v(279.45, 1.85) * mm, "end": v(280.15, 1.85) * mm});
            skArc(sketch, "E25.66.11.0", {"start": v(281, 2.63) * mm, "mid": v(280.5, 2.33) * mm, "end": v(280.15, 1.85) * mm});
            skArc(sketch, "E25.70.11.0", {"start": v(280.15, 0.75) * mm, "mid": v(280.5, 0.27) * mm, "end": v(281, -0.03) * mm});
            skLineSegment(sketch, "E25.74.11.0", {"start": v(279.45, 1.85) * mm, "end": v(279.45, 0.75) * mm});
            skLineSegment(sketch, "E25.0.12.0", {"start": v(293.56, 1.3) * mm, "end": v(306.44, 1.3) * mm, "construction": true});
            skLineSegment(sketch, "E25.3.12.0", {"start": v(294, -3.5) * mm, "end": v(294, -0.03) * mm});
            skLineSegment(sketch, "E25.6.12.0", {"start": v(306, -3.5) * mm, "end": v(306, -0.03) * mm});
            skLineSegment(sketch, "E25.9.12.0", {"start": v(305.5, -4) * mm, "end": v(294.5, -4) * mm});
            skLineSegment(sketch, "E25.12.12.0", {"start": v(305.5, 4) * mm, "end": v(294.5, 4) * mm});
            skPoint(sketch, "E25.15.12.0", {"position": v(300, 0) * mm});
            skPoint(sketch, "E25.16.12.0", {"position": v(294, -4) * mm});
            skPoint(sketch, "E25.17.12.0", {"position": v(294, 4) * mm});
            skPoint(sketch, "E25.18.12.0", {"position": v(306, 4) * mm});
            skPoint(sketch, "E25.19.12.0", {"position": v(306, -4) * mm});
            skPoint(sketch, "E25.20.12.0", {"position": v(300, 0) * mm});
            skLineSegment(sketch, "E25.21.12.0", {"start": v(306, -3.5) * mm, "end": v(305.5, -4) * mm});
            skLineSegment(sketch, "E25.24.12.0", {"start": v(306, 3.5) * mm, "end": v(305.5, 4) * mm});
            skLineSegment(sketch, "E25.27.12.0", {"start": v(294, -3.5) * mm, "end": v(294.5, -4) * mm});
            skLineSegment(sketch, "E25.30.12.0", {"start": v(295.55, 1.85) * mm, "end": v(294.85, 1.85) * mm});
            skLineSegment(sketch, "E25.33.12.0", {"start": v(294, 2.63) * mm, "end": v(294, 3.5) * mm});
            skLineSegment(sketch, "E25.36.12.0", {"start": v(306, 2.63) * mm, "end": v(306, 3.5) * mm});
            skArc(sketch, "E25.39.12.0", {"start": v(305.15, 0.75) * mm, "mid": v(305.5, 0.27) * mm, "end": v(306, -0.03) * mm});
            skLineSegment(sketch, "E25.43.12.0", {"start": v(295.55, 1.85) * mm, "end": v(295.55, 0.75) * mm});
            skLineSegment(sketch, "E25.46.12.0", {"start": v(304.45, 0.75) * mm, "end": v(305.15, 0.75) * mm});
            skLineSegment(sketch, "E25.49.12.0", {"start": v(295.55, 0.75) * mm, "end": v(294.85, 0.75) * mm});
            skArc(sketch, "E25.52.12.0", {"start": v(294, -0.03) * mm, "mid": v(294.5, 0.27) * mm, "end": v(294.85, 0.75) * mm});
            skLineSegment(sketch, "E25.56.12.0", {"start": v(294, 3.5) * mm, "end": v(294.5, 4) * mm});
            skArc(sketch, "E25.59.12.0", {"start": v(294.85, 1.85) * mm, "mid": v(294.5, 2.33) * mm, "end": v(294, 2.63) * mm});
            skLineSegment(sketch, "E25.63.12.0", {"start": v(304.45, 1.85) * mm, "end": v(305.15, 1.85) * mm});
            skArc(sketch, "E25.66.12.0", {"start": v(306, 2.63) * mm, "mid": v(305.5, 2.33) * mm, "end": v(305.15, 1.85) * mm});
            skArc(sketch, "E25.70.12.0", {"start": v(305.15, 0.75) * mm, "mid": v(305.5, 0.27) * mm, "end": v(306, -0.03) * mm});
            skLineSegment(sketch, "E25.74.12.0", {"start": v(304.45, 1.85) * mm, "end": v(304.45, 0.75) * mm});
            skLineSegment(sketch, "E25.0.13.0", {"start": v(318.56, 1.3) * mm, "end": v(331.44, 1.3) * mm, "construction": true});
            skLineSegment(sketch, "E25.3.13.0", {"start": v(319, -3.5) * mm, "end": v(319, -0.03) * mm});
            skLineSegment(sketch, "E25.6.13.0", {"start": v(331, -3.5) * mm, "end": v(331, -0.03) * mm});
            skLineSegment(sketch, "E25.9.13.0", {"start": v(330.5, -4) * mm, "end": v(319.5, -4) * mm});
            skLineSegment(sketch, "E25.12.13.0", {"start": v(330.5, 4) * mm, "end": v(319.5, 4) * mm});
            skPoint(sketch, "E25.15.13.0", {"position": v(325, 0) * mm});
            skPoint(sketch, "E25.16.13.0", {"position": v(319, -4) * mm});
            skPoint(sketch, "E25.17.13.0", {"position": v(319, 4) * mm});
            skPoint(sketch, "E25.18.13.0", {"position": v(331, 4) * mm});
            skPoint(sketch, "E25.19.13.0", {"position": v(331, -4) * mm});
            skPoint(sketch, "E25.20.13.0", {"position": v(325, 0) * mm});
            skLineSegment(sketch, "E25.21.13.0", {"start": v(331, -3.5) * mm, "end": v(330.5, -4) * mm});
            skLineSegment(sketch, "E25.24.13.0", {"start": v(331, 3.5) * mm, "end": v(330.5, 4) * mm});
            skLineSegment(sketch, "E25.27.13.0", {"start": v(319, -3.5) * mm, "end": v(319.5, -4) * mm});
            skLineSegment(sketch, "E25.30.13.0", {"start": v(320.55, 1.85) * mm, "end": v(319.85, 1.85) * mm});
            skLineSegment(sketch, "E25.33.13.0", {"start": v(319, 2.63) * mm, "end": v(319, 3.5) * mm});
            skLineSegment(sketch, "E25.36.13.0", {"start": v(331, 2.63) * mm, "end": v(331, 3.5) * mm});
            skArc(sketch, "E25.39.13.0", {"start": v(330.15, 0.75) * mm, "mid": v(330.5, 0.27) * mm, "end": v(331, -0.03) * mm});
            skLineSegment(sketch, "E25.43.13.0", {"start": v(320.55, 1.85) * mm, "end": v(320.55, 0.75) * mm});
            skLineSegment(sketch, "E25.46.13.0", {"start": v(329.45, 0.75) * mm, "end": v(330.15, 0.75) * mm});
            skLineSegment(sketch, "E25.49.13.0", {"start": v(320.55, 0.75) * mm, "end": v(319.85, 0.75) * mm});
            skArc(sketch, "E25.52.13.0", {"start": v(319, -0.03) * mm, "mid": v(319.5, 0.27) * mm, "end": v(319.85, 0.75) * mm});
            skLineSegment(sketch, "E25.56.13.0", {"start": v(319, 3.5) * mm, "end": v(319.5, 4) * mm});
            skArc(sketch, "E25.59.13.0", {"start": v(319.85, 1.85) * mm, "mid": v(319.5, 2.33) * mm, "end": v(319, 2.63) * mm});
            skLineSegment(sketch, "E25.63.13.0", {"start": v(329.45, 1.85) * mm, "end": v(330.15, 1.85) * mm});
            skArc(sketch, "E25.66.13.0", {"start": v(331, 2.63) * mm, "mid": v(330.5, 2.33) * mm, "end": v(330.15, 1.85) * mm});
            skArc(sketch, "E25.70.13.0", {"start": v(330.15, 0.75) * mm, "mid": v(330.5, 0.27) * mm, "end": v(331, -0.03) * mm});
            skLineSegment(sketch, "E25.74.13.0", {"start": v(329.45, 1.85) * mm, "end": v(329.45, 0.75) * mm});
            skLineSegment(sketch, "E25.0.14.0", {"start": v(343.56, 1.3) * mm, "end": v(356.44, 1.3) * mm, "construction": true});
            skLineSegment(sketch, "E25.3.14.0", {"start": v(344, -3.5) * mm, "end": v(344, -0.03) * mm});
            skLineSegment(sketch, "E25.6.14.0", {"start": v(356, -3.5) * mm, "end": v(356, -0.03) * mm});
            skLineSegment(sketch, "E25.9.14.0", {"start": v(355.5, -4) * mm, "end": v(344.5, -4) * mm});
            skLineSegment(sketch, "E25.12.14.0", {"start": v(355.5, 4) * mm, "end": v(344.5, 4) * mm});
            skPoint(sketch, "E25.15.14.0", {"position": v(350, 0) * mm});
            skPoint(sketch, "E25.16.14.0", {"position": v(344, -4) * mm});
            skPoint(sketch, "E25.17.14.0", {"position": v(344, 4) * mm});
            skPoint(sketch, "E25.18.14.0", {"position": v(356, 4) * mm});
            skPoint(sketch, "E25.19.14.0", {"position": v(356, -4) * mm});
            skPoint(sketch, "E25.20.14.0", {"position": v(350, 0) * mm});
            skLineSegment(sketch, "E25.21.14.0", {"start": v(356, -3.5) * mm, "end": v(355.5, -4) * mm});
            skLineSegment(sketch, "E25.24.14.0", {"start": v(356, 3.5) * mm, "end": v(355.5, 4) * mm});
            skLineSegment(sketch, "E25.27.14.0", {"start": v(344, -3.5) * mm, "end": v(344.5, -4) * mm});
            skLineSegment(sketch, "E25.30.14.0", {"start": v(345.55, 1.85) * mm, "end": v(344.85, 1.85) * mm});
            skLineSegment(sketch, "E25.33.14.0", {"start": v(344, 2.63) * mm, "end": v(344, 3.5) * mm});
            skLineSegment(sketch, "E25.36.14.0", {"start": v(356, 2.63) * mm, "end": v(356, 3.5) * mm});
            skArc(sketch, "E25.39.14.0", {"start": v(355.15, 0.75) * mm, "mid": v(355.5, 0.27) * mm, "end": v(356, -0.03) * mm});
            skLineSegment(sketch, "E25.43.14.0", {"start": v(345.55, 1.85) * mm, "end": v(345.55, 0.75) * mm});
            skLineSegment(sketch, "E25.46.14.0", {"start": v(354.45, 0.75) * mm, "end": v(355.15, 0.75) * mm});
            skLineSegment(sketch, "E25.49.14.0", {"start": v(345.55, 0.75) * mm, "end": v(344.85, 0.75) * mm});
            skArc(sketch, "E25.52.14.0", {"start": v(344, -0.03) * mm, "mid": v(344.5, 0.27) * mm, "end": v(344.85, 0.75) * mm});
            skLineSegment(sketch, "E25.56.14.0", {"start": v(344, 3.5) * mm, "end": v(344.5, 4) * mm});
            skArc(sketch, "E25.59.14.0", {"start": v(344.85, 1.85) * mm, "mid": v(344.5, 2.33) * mm, "end": v(344, 2.63) * mm});
            skLineSegment(sketch, "E25.63.14.0", {"start": v(354.45, 1.85) * mm, "end": v(355.15, 1.85) * mm});
            skArc(sketch, "E25.66.14.0", {"start": v(356, 2.63) * mm, "mid": v(355.5, 2.33) * mm, "end": v(355.15, 1.85) * mm});
            skArc(sketch, "E25.70.14.0", {"start": v(355.15, 0.75) * mm, "mid": v(355.5, 0.27) * mm, "end": v(356, -0.03) * mm});
            skLineSegment(sketch, "E25.74.14.0", {"start": v(354.45, 1.85) * mm, "end": v(354.45, 0.75) * mm});
            skSolve(sketch);
        }
        {
            var Q0;
            Q0=makeQuery(id+"F0.imprint","IMPRINT",FACE,{"disambiguationData":[TD([[makeQuery(id+"F0.imprint","IMPRINT",EDGE,{"derivedFrom":sQuery(id+"F0.wireOp",EDGE,"E1.bottom")}),-1.0]])]});
            extrude(context, id + "F1", {"entities" : qUnion([Q0]), "depth" : 70 * mm, "offsetDistance" : 25 * mm});
        }
        {
            var Q0;
            Q0=makeQuery(id+"F0.imprint","IMPRINT",FACE,{"disambiguationData":[TD([[makeQuery(id+"F0.imprint","IMPRINT",EDGE,{"derivedFrom":sQuery(id+"F0.wireOp",EDGE,"E23.1.0.1")}),-1.0]])]});
            extrude(context, id + "F2", {"entities" : qUnion([Q0]), "depth" : 95 * mm, "offsetDistance" : 25 * mm});
        }
        {
            var Q0;
            Q0=makeQuery(id+"F0.imprint","IMPRINT",FACE,{"disambiguationData":[TD([[makeQuery(id+"F0.imprint","IMPRINT",EDGE,{"derivedFrom":sQuery(id+"F0.wireOp",EDGE,"E23.2.0.1")}),-1.0]])]});
            extrude(context, id + "F3", {"entities" : qUnion([Q0]), "depth" : 120 * mm, "offsetDistance" : 25 * mm});
        }
        {
            var Q0;
            Q0=makeQuery(id+"F0.imprint","IMPRINT",FACE,{"disambiguationData":[TD([[makeQuery(id+"F0.imprint","IMPRINT",EDGE,{"derivedFrom":sQuery(id+"F0.wireOp",EDGE,"E23.3.0.1")}),-1.0]])]});
            extrude(context, id + "F4", {"entities" : qUnion([Q0]), "depth" : 145 * mm, "offsetDistance" : 25 * mm});
        }
        {
            var Q0;
            Q0=makeQuery(id+"F0.imprint","IMPRINT",FACE,{"disambiguationData":[TD([[makeQuery(id+"F0.imprint","IMPRINT",EDGE,{"derivedFrom":sQuery(id+"F0.wireOp",EDGE,"E23.4.0.1")}),-1.0]])]});
            extrude(context, id + "F5", {"entities" : qUnion([Q0]), "depth" : 170 * mm, "offsetDistance" : 25 * mm});
        }
        {
            var Q0;
            Q0=makeQuery(id+"F0.imprint","IMPRINT",FACE,{"disambiguationData":[TD([[makeQuery(id+"F0.imprint","IMPRINT",EDGE,{"derivedFrom":sQuery(id+"F0.wireOp",EDGE,"E23.5.0.1")}),-1.0]])]});
            extrude(context, id + "F6", {"entities" : qUnion([Q0]), "depth" : 195 * mm, "offsetDistance" : 25 * mm});
        }
        {
            var Q0;
            Q0=makeQuery(id+"F0.imprint","IMPRINT",FACE,{"disambiguationData":[TD([[makeQuery(id+"F0.imprint","IMPRINT",EDGE,{"derivedFrom":sQuery(id+"F0.wireOp",EDGE,"E23.6.0.1")}),-1.0]])]});
            extrude(context, id + "F7", {"entities" : qUnion([Q0]), "depth" : 220 * mm, "offsetDistance" : 25 * mm});
        }
        {
            var Q0;
            Q0=makeQuery(id+"F0.imprint","IMPRINT",FACE,{"disambiguationData":[TD([[makeQuery(id+"F0.imprint","IMPRINT",EDGE,{"derivedFrom":sQuery(id+"F0.wireOp",EDGE,"E24.3.7.0")}),-1.0]])]});
            extrude(context, id + "F8", {"entities" : qUnion([Q0]), "depth" : 245 * mm, "offsetDistance" : 25 * mm});
        }
        {
            var Q0;
            Q0=makeQuery(id+"F0.imprint","IMPRINT",FACE,{"disambiguationData":[TD([[makeQuery(id+"F0.imprint","IMPRINT",EDGE,{"derivedFrom":sQuery(id+"F0.wireOp",EDGE,"E24.3.8.0")}),-1.0]])]});
            extrude(context, id + "F9", {"entities" : qUnion([Q0]), "depth" : 270 * mm, "offsetDistance" : 25 * mm});
        }
        {
            var Q0;
            Q0=makeQuery(id+"F0.imprint","IMPRINT",FACE,{"disambiguationData":[TD([[makeQuery(id+"F0.imprint","IMPRINT",EDGE,{"derivedFrom":sQuery(id+"F0.wireOp",EDGE,"E24.3.9.0")}),-1.0]])]});
            extrude(context, id + "F10", {"entities" : qUnion([Q0]), "depth" : 320 * mm, "offsetDistance" : 25 * mm});
        }
        {
            var Q0;
            Q0=makeQuery(id+"F0.imprint","IMPRINT",FACE,{"disambiguationData":[TD([[makeQuery(id+"F0.imprint","IMPRINT",EDGE,{"derivedFrom":sQuery(id+"F0.wireOp",EDGE,"E24.3.10.0")}),-1.0]])]});
            extrude(context, id + "F11", {"entities" : qUnion([Q0]), "depth" : 370 * mm, "offsetDistance" : 25 * mm});
        }
        {
            var Q0;
            Q0=makeQuery(id+"F0.imprint","IMPRINT",FACE,{"disambiguationData":[TD([[makeQuery(id+"F0.imprint","IMPRINT",EDGE,{"derivedFrom":sQuery(id+"F0.wireOp",EDGE,"E25.3.11.0")}),-1.0]])]});
            extrude(context, id + "F12", {"entities" : qUnion([Q0]), "depth" : 470 * mm, "offsetDistance" : 25 * mm});
        }
        {
            var Q0;
            Q0=makeQuery(id+"F0.imprint","IMPRINT",FACE,{"disambiguationData":[TD([[makeQuery(id+"F0.imprint","IMPRINT",EDGE,{"derivedFrom":sQuery(id+"F0.wireOp",EDGE,"E25.3.12.0")}),-1.0]])]});
            extrude(context, id + "F13", {"entities" : qUnion([Q0]), "depth" : 570 * mm, "offsetDistance" : 25 * mm});
        }
        {
            var Q0;
            Q0=makeQuery(id+"F0.imprint","IMPRINT",FACE,{"disambiguationData":[TD([[makeQuery(id+"F0.imprint","IMPRINT",EDGE,{"derivedFrom":sQuery(id+"F0.wireOp",EDGE,"E25.3.13.0")}),-1.0]])]});
            extrude(context, id + "F14", {"entities" : qUnion([Q0]), "depth" : 695 * mm, "offsetDistance" : 25 * mm});
        }
        {
            var Q0;
            Q0=makeQuery(id+"F0.imprint","IMPRINT",FACE,{"disambiguationData":[TD([[makeQuery(id+"F0.imprint","IMPRINT",EDGE,{"derivedFrom":sQuery(id+"F0.wireOp",EDGE,"E25.3.14.0")}),-1.0]])]});
            extrude(context, id + "F15", {"entities" : qUnion([Q0]), "depth" : 1995 * mm, "offsetDistance" : 25 * mm});
        }
        {
            var Q0;
            Q0=makeQuery(id+"F1.opExtrude","SWEPT_FACE",FACE,{"disambiguationData":[OSD([sQuery(id+"F0.wireOp",EDGE,"E1.top")])]});
            var sketch = newSketch(context, id + "F16", { "sketchPlane" : qUnion([Q0])});
            skPoint(sketch, "E26", {"position": v(0, -10) * mm});
            skPoint(sketch, "E27.1.0.0", {"position": v(25, -10) * mm});
            skPoint(sketch, "E27.2.0.0", {"position": v(50, -10) * mm});
            skPoint(sketch, "E27.3.0.0", {"position": v(75, -10) * mm});
            skPoint(sketch, "E27.4.0.0", {"position": v(100, -10) * mm});
            skPoint(sketch, "E27.5.0.0", {"position": v(125, -10) * mm});
            skPoint(sketch, "E27.6.0.0", {"position": v(150, -10) * mm});
            skLineSegment(sketch, "E27.direction1", {"start": v(0, -10) * mm, "end": v(25, -10) * mm, "construction": true});
            skPoint(sketch, "E28.1.0.0", {"position": v(0, -35) * mm});
            skPoint(sketch, "E28.1.0.1", {"position": v(25, -35) * mm});
            skPoint(sketch, "E28.1.0.2", {"position": v(50, -35) * mm});
            skPoint(sketch, "E28.1.0.3", {"position": v(75, -35) * mm});
            skPoint(sketch, "E28.1.0.4", {"position": v(100, -35) * mm});
            skPoint(sketch, "E28.1.0.5", {"position": v(125, -35) * mm});
            skPoint(sketch, "E28.1.0.6", {"position": v(150, -35) * mm});
            skPoint(sketch, "E28.2.0.0", {"position": v(0, -60) * mm});
            skPoint(sketch, "E28.2.0.1", {"position": v(25, -60) * mm});
            skPoint(sketch, "E28.2.0.2", {"position": v(50, -60) * mm});
            skPoint(sketch, "E28.2.0.3", {"position": v(75, -60) * mm});
            skPoint(sketch, "E28.2.0.4", {"position": v(100, -60) * mm});
            skPoint(sketch, "E28.2.0.5", {"position": v(125, -60) * mm});
            skPoint(sketch, "E28.2.0.6", {"position": v(150, -60) * mm});
            skPoint(sketch, "E28.3.0.0", {"position": v(0, -85) * mm});
            skPoint(sketch, "E28.3.0.1", {"position": v(25, -85) * mm});
            skPoint(sketch, "E28.3.0.2", {"position": v(50, -85) * mm});
            skPoint(sketch, "E28.3.0.3", {"position": v(75, -85) * mm});
            skPoint(sketch, "E28.3.0.4", {"position": v(100, -85) * mm});
            skPoint(sketch, "E28.3.0.5", {"position": v(125, -85) * mm});
            skPoint(sketch, "E28.3.0.6", {"position": v(150, -85) * mm});
            skPoint(sketch, "E28.4.0.0", {"position": v(0, -110) * mm});
            skPoint(sketch, "E28.4.0.1", {"position": v(25, -110) * mm});
            skPoint(sketch, "E28.4.0.2", {"position": v(50, -110) * mm});
            skPoint(sketch, "E28.4.0.3", {"position": v(75, -110) * mm});
            skPoint(sketch, "E28.4.0.4", {"position": v(100, -110) * mm});
            skPoint(sketch, "E28.4.0.5", {"position": v(125, -110) * mm});
            skPoint(sketch, "E28.4.0.6", {"position": v(150, -110) * mm});
            skPoint(sketch, "E28.5.0.0", {"position": v(0, -135) * mm});
            skPoint(sketch, "E28.5.0.1", {"position": v(25, -135) * mm});
            skPoint(sketch, "E28.5.0.2", {"position": v(50, -135) * mm});
            skPoint(sketch, "E28.5.0.3", {"position": v(75, -135) * mm});
            skPoint(sketch, "E28.5.0.4", {"position": v(100, -135) * mm});
            skPoint(sketch, "E28.5.0.5", {"position": v(125, -135) * mm});
            skPoint(sketch, "E28.5.0.6", {"position": v(150, -135) * mm});
            skPoint(sketch, "E28.6.0.0", {"position": v(0, -160) * mm});
            skPoint(sketch, "E28.6.0.1", {"position": v(25, -160) * mm});
            skPoint(sketch, "E28.6.0.2", {"position": v(50, -160) * mm});
            skPoint(sketch, "E28.6.0.3", {"position": v(75, -160) * mm});
            skPoint(sketch, "E28.6.0.4", {"position": v(100, -160) * mm});
            skPoint(sketch, "E28.6.0.5", {"position": v(125, -160) * mm});
            skPoint(sketch, "E28.6.0.6", {"position": v(150, -160) * mm});
            skPoint(sketch, "E28.7.0.0", {"position": v(0, -185) * mm});
            skPoint(sketch, "E28.7.0.1", {"position": v(25, -185) * mm});
            skPoint(sketch, "E28.7.0.2", {"position": v(50, -185) * mm});
            skPoint(sketch, "E28.7.0.3", {"position": v(75, -185) * mm});
            skPoint(sketch, "E28.7.0.4", {"position": v(100, -185) * mm});
            skPoint(sketch, "E28.7.0.5", {"position": v(125, -185) * mm});
            skPoint(sketch, "E28.7.0.6", {"position": v(150, -185) * mm});
            skPoint(sketch, "E28.8.0.0", {"position": v(0, -210) * mm});
            skPoint(sketch, "E28.8.0.1", {"position": v(25, -210) * mm});
            skPoint(sketch, "E28.8.0.2", {"position": v(50, -210) * mm});
            skPoint(sketch, "E28.8.0.3", {"position": v(75, -210) * mm});
            skPoint(sketch, "E28.8.0.4", {"position": v(100, -210) * mm});
            skPoint(sketch, "E28.8.0.5", {"position": v(125, -210) * mm});
            skPoint(sketch, "E28.8.0.6", {"position": v(150, -210) * mm});
            skLineSegment(sketch, "E28.direction1", {"start": v(0, -10) * mm, "end": v(0, -35) * mm, "construction": true});
            skPoint(sketch, "E29.0.7.0", {"position": v(175, -10) * mm});
            skPoint(sketch, "E29.0.8.0", {"position": v(200, -10) * mm});
            skPoint(sketch, "E29.0.9.0", {"position": v(225, -10) * mm});
            skPoint(sketch, "E29.0.10.0", {"position": v(250, -10) * mm});
            skPoint(sketch, "E30.1.0.0", {"position": v(250, -35) * mm});
            skPoint(sketch, "E30.1.0.1", {"position": v(225, -35) * mm});
            skPoint(sketch, "E30.1.0.2", {"position": v(200, -35) * mm});
            skPoint(sketch, "E30.1.0.3", {"position": v(175, -35) * mm});
            skPoint(sketch, "E30.2.0.0", {"position": v(250, -60) * mm});
            skPoint(sketch, "E30.2.0.1", {"position": v(225, -60) * mm});
            skPoint(sketch, "E30.2.0.2", {"position": v(200, -60) * mm});
            skPoint(sketch, "E30.2.0.3", {"position": v(175, -60) * mm});
            skLineSegment(sketch, "E30.direction1", {"start": v(175, -10) * mm, "end": v(175, -35) * mm, "construction": true});
            skPoint(sketch, "E31.0.3.0", {"position": v(250, -85) * mm});
            skPoint(sketch, "E31.1.3.0", {"position": v(225, -85) * mm});
            skPoint(sketch, "E31.2.3.0", {"position": v(200, -85) * mm});
            skPoint(sketch, "E31.3.3.0", {"position": v(175, -85) * mm});
            skPoint(sketch, "E31.0.4.0", {"position": v(250, -110) * mm});
            skPoint(sketch, "E31.1.4.0", {"position": v(225, -110) * mm});
            skPoint(sketch, "E31.2.4.0", {"position": v(200, -110) * mm});
            skPoint(sketch, "E31.3.4.0", {"position": v(175, -110) * mm});
            skPoint(sketch, "E31.0.5.0", {"position": v(250, -135) * mm});
            skPoint(sketch, "E31.1.5.0", {"position": v(225, -135) * mm});
            skPoint(sketch, "E31.2.5.0", {"position": v(200, -135) * mm});
            skPoint(sketch, "E31.3.5.0", {"position": v(175, -135) * mm});
            skPoint(sketch, "E31.0.6.0", {"position": v(250, -160) * mm});
            skPoint(sketch, "E31.1.6.0", {"position": v(225, -160) * mm});
            skPoint(sketch, "E31.2.6.0", {"position": v(200, -160) * mm});
            skPoint(sketch, "E31.3.6.0", {"position": v(175, -160) * mm});
            skPoint(sketch, "E31.0.7.0", {"position": v(250, -185) * mm});
            skPoint(sketch, "E31.1.7.0", {"position": v(225, -185) * mm});
            skPoint(sketch, "E31.2.7.0", {"position": v(200, -185) * mm});
            skPoint(sketch, "E31.3.7.0", {"position": v(175, -185) * mm});
            skPoint(sketch, "E31.0.8.0", {"position": v(250, -210) * mm});
            skPoint(sketch, "E31.1.8.0", {"position": v(225, -210) * mm});
            skPoint(sketch, "E31.2.8.0", {"position": v(200, -210) * mm});
            skPoint(sketch, "E31.3.8.0", {"position": v(175, -210) * mm});
            skPoint(sketch, "E31.0.9.0", {"position": v(250, -235) * mm});
            skPoint(sketch, "E31.1.9.0", {"position": v(225, -235) * mm});
            skPoint(sketch, "E31.2.9.0", {"position": v(200, -235) * mm});
            skPoint(sketch, "E31.3.9.0", {"position": v(175, -235) * mm});
            skPoint(sketch, "E31.0.10.0", {"position": v(250, -260) * mm});
            skPoint(sketch, "E31.1.10.0", {"position": v(225, -260) * mm});
            skPoint(sketch, "E31.2.10.0", {"position": v(200, -260) * mm});
            skPoint(sketch, "E31.3.10.0", {"position": v(175, -260) * mm});
            skPoint(sketch, "E31.0.11.0", {"position": v(250, -285) * mm});
            skPoint(sketch, "E31.1.11.0", {"position": v(225, -285) * mm});
            skPoint(sketch, "E31.2.11.0", {"position": v(200, -285) * mm});
            skPoint(sketch, "E31.3.11.0", {"position": v(175, -285) * mm});
            skPoint(sketch, "E31.0.12.0", {"position": v(250, -310) * mm});
            skPoint(sketch, "E31.1.12.0", {"position": v(225, -310) * mm});
            skPoint(sketch, "E31.2.12.0", {"position": v(200, -310) * mm});
            skPoint(sketch, "E31.3.12.0", {"position": v(175, -310) * mm});
            skPoint(sketch, "E31.0.13.0", {"position": v(250, -335) * mm});
            skPoint(sketch, "E31.1.13.0", {"position": v(225, -335) * mm});
            skPoint(sketch, "E31.2.13.0", {"position": v(200, -335) * mm});
            skPoint(sketch, "E31.3.13.0", {"position": v(175, -335) * mm});
            skPoint(sketch, "E31.0.14.0", {"position": v(250, -360) * mm});
            skPoint(sketch, "E31.1.14.0", {"position": v(225, -360) * mm});
            skPoint(sketch, "E31.2.14.0", {"position": v(200, -360) * mm});
            skPoint(sketch, "E31.3.14.0", {"position": v(175, -360) * mm});
            skPoint(sketch, "E32.0.11.0", {"position": v(275, -10) * mm});
            skPoint(sketch, "E32.0.12.0", {"position": v(300, -10) * mm});
            skPoint(sketch, "E32.0.13.0", {"position": v(325, -10) * mm});
            skPoint(sketch, "E32.0.14.0", {"position": v(350, -10) * mm});
            skPoint(sketch, "E33.1.0.0", {"position": v(350, -35) * mm});
            skPoint(sketch, "E33.1.0.1", {"position": v(275, -35) * mm});
            skPoint(sketch, "E33.1.0.2", {"position": v(325, -35) * mm});
            skPoint(sketch, "E33.1.0.3", {"position": v(300, -35) * mm});
            skPoint(sketch, "E33.2.0.0", {"position": v(350, -60) * mm});
            skPoint(sketch, "E33.2.0.1", {"position": v(275, -60) * mm});
            skPoint(sketch, "E33.2.0.2", {"position": v(325, -60) * mm});
            skPoint(sketch, "E33.2.0.3", {"position": v(300, -60) * mm});
            skLineSegment(sketch, "E33.direction1", {"start": v(275, -10) * mm, "end": v(275, -35) * mm, "construction": true});
            skPoint(sketch, "E34.0.3.0", {"position": v(350, -85) * mm});
            skPoint(sketch, "E34.1.3.0", {"position": v(275, -85) * mm});
            skPoint(sketch, "E34.2.3.0", {"position": v(325, -85) * mm});
            skPoint(sketch, "E34.3.3.0", {"position": v(300, -85) * mm});
            skPoint(sketch, "E34.0.4.0", {"position": v(350, -110) * mm});
            skPoint(sketch, "E34.1.4.0", {"position": v(275, -110) * mm});
            skPoint(sketch, "E34.2.4.0", {"position": v(325, -110) * mm});
            skPoint(sketch, "E34.3.4.0", {"position": v(300, -110) * mm});
            skPoint(sketch, "E34.0.5.0", {"position": v(350, -135) * mm});
            skPoint(sketch, "E34.1.5.0", {"position": v(275, -135) * mm});
            skPoint(sketch, "E34.2.5.0", {"position": v(325, -135) * mm});
            skPoint(sketch, "E34.3.5.0", {"position": v(300, -135) * mm});
            skPoint(sketch, "E34.0.6.0", {"position": v(350, -160) * mm});
            skPoint(sketch, "E34.1.6.0", {"position": v(275, -160) * mm});
            skPoint(sketch, "E34.2.6.0", {"position": v(325, -160) * mm});
            skPoint(sketch, "E34.3.6.0", {"position": v(300, -160) * mm});
            skPoint(sketch, "E34.0.7.0", {"position": v(350, -185) * mm});
            skPoint(sketch, "E34.1.7.0", {"position": v(275, -185) * mm});
            skPoint(sketch, "E34.2.7.0", {"position": v(325, -185) * mm});
            skPoint(sketch, "E34.3.7.0", {"position": v(300, -185) * mm});
            skPoint(sketch, "E34.0.8.0", {"position": v(350, -210) * mm});
            skPoint(sketch, "E34.1.8.0", {"position": v(275, -210) * mm});
            skPoint(sketch, "E34.2.8.0", {"position": v(325, -210) * mm});
            skPoint(sketch, "E34.3.8.0", {"position": v(300, -210) * mm});
            skPoint(sketch, "E34.0.9.0", {"position": v(350, -235) * mm});
            skPoint(sketch, "E34.1.9.0", {"position": v(275, -235) * mm});
            skPoint(sketch, "E34.2.9.0", {"position": v(325, -235) * mm});
            skPoint(sketch, "E34.3.9.0", {"position": v(300, -235) * mm});
            skPoint(sketch, "E34.0.10.0", {"position": v(350, -260) * mm});
            skPoint(sketch, "E34.1.10.0", {"position": v(275, -260) * mm});
            skPoint(sketch, "E34.2.10.0", {"position": v(325, -260) * mm});
            skPoint(sketch, "E34.3.10.0", {"position": v(300, -260) * mm});
            skPoint(sketch, "E34.0.11.0", {"position": v(350, -285) * mm});
            skPoint(sketch, "E34.1.11.0", {"position": v(275, -285) * mm});
            skPoint(sketch, "E34.2.11.0", {"position": v(325, -285) * mm});
            skPoint(sketch, "E34.3.11.0", {"position": v(300, -285) * mm});
            skPoint(sketch, "E34.0.12.0", {"position": v(350, -310) * mm});
            skPoint(sketch, "E34.1.12.0", {"position": v(275, -310) * mm});
            skPoint(sketch, "E34.2.12.0", {"position": v(325, -310) * mm});
            skPoint(sketch, "E34.3.12.0", {"position": v(300, -310) * mm});
            skPoint(sketch, "E34.0.13.0", {"position": v(350, -335) * mm});
            skPoint(sketch, "E34.1.13.0", {"position": v(275, -335) * mm});
            skPoint(sketch, "E34.2.13.0", {"position": v(325, -335) * mm});
            skPoint(sketch, "E34.3.13.0", {"position": v(300, -335) * mm});
            skPoint(sketch, "E34.0.14.0", {"position": v(350, -360) * mm});
            skPoint(sketch, "E34.1.14.0", {"position": v(275, -360) * mm});
            skPoint(sketch, "E34.2.14.0", {"position": v(325, -360) * mm});
            skPoint(sketch, "E34.3.14.0", {"position": v(300, -360) * mm});
            skPoint(sketch, "E34.0.15.0", {"position": v(350, -385) * mm});
            skPoint(sketch, "E34.1.15.0", {"position": v(275, -385) * mm});
            skPoint(sketch, "E34.2.15.0", {"position": v(325, -385) * mm});
            skPoint(sketch, "E34.3.15.0", {"position": v(300, -385) * mm});
            skPoint(sketch, "E34.0.16.0", {"position": v(350, -410) * mm});
            skPoint(sketch, "E34.1.16.0", {"position": v(275, -410) * mm});
            skPoint(sketch, "E34.2.16.0", {"position": v(325, -410) * mm});
            skPoint(sketch, "E34.3.16.0", {"position": v(300, -410) * mm});
            skPoint(sketch, "E34.0.17.0", {"position": v(350, -435) * mm});
            skPoint(sketch, "E34.1.17.0", {"position": v(275, -435) * mm});
            skPoint(sketch, "E34.2.17.0", {"position": v(325, -435) * mm});
            skPoint(sketch, "E34.3.17.0", {"position": v(300, -435) * mm});
            skPoint(sketch, "E34.0.18.0", {"position": v(350, -460) * mm});
            skPoint(sketch, "E34.1.18.0", {"position": v(275, -460) * mm});
            skPoint(sketch, "E34.2.18.0", {"position": v(325, -460) * mm});
            skPoint(sketch, "E34.3.18.0", {"position": v(300, -460) * mm});
            skPoint(sketch, "E34.0.19.0", {"position": v(350, -485) * mm});
            skPoint(sketch, "E34.1.19.0", {"position": v(275, -485) * mm});
            skPoint(sketch, "E34.2.19.0", {"position": v(325, -485) * mm});
            skPoint(sketch, "E34.3.19.0", {"position": v(300, -485) * mm});
            skPoint(sketch, "E34.0.20.0", {"position": v(350, -510) * mm});
            skPoint(sketch, "E34.1.20.0", {"position": v(275, -510) * mm});
            skPoint(sketch, "E34.2.20.0", {"position": v(325, -510) * mm});
            skPoint(sketch, "E34.3.20.0", {"position": v(300, -510) * mm});
            skPoint(sketch, "E34.0.21.0", {"position": v(350, -535) * mm});
            skPoint(sketch, "E34.1.21.0", {"position": v(275, -535) * mm});
            skPoint(sketch, "E34.2.21.0", {"position": v(325, -535) * mm});
            skPoint(sketch, "E34.3.21.0", {"position": v(300, -535) * mm});
            skPoint(sketch, "E34.0.22.0", {"position": v(350, -560) * mm});
            skPoint(sketch, "E34.1.22.0", {"position": v(275, -560) * mm});
            skPoint(sketch, "E34.2.22.0", {"position": v(325, -560) * mm});
            skPoint(sketch, "E34.3.22.0", {"position": v(300, -560) * mm});
            skPoint(sketch, "E34.0.23.0", {"position": v(350, -585) * mm});
            skPoint(sketch, "E34.1.23.0", {"position": v(275, -585) * mm});
            skPoint(sketch, "E34.2.23.0", {"position": v(325, -585) * mm});
            skPoint(sketch, "E34.3.23.0", {"position": v(300, -585) * mm});
            skPoint(sketch, "E34.0.24.0", {"position": v(350, -610) * mm});
            skPoint(sketch, "E34.1.24.0", {"position": v(275, -610) * mm});
            skPoint(sketch, "E34.2.24.0", {"position": v(325, -610) * mm});
            skPoint(sketch, "E34.3.24.0", {"position": v(300, -610) * mm});
            skPoint(sketch, "E34.0.25.0", {"position": v(350, -635) * mm});
            skPoint(sketch, "E34.1.25.0", {"position": v(275, -635) * mm});
            skPoint(sketch, "E34.2.25.0", {"position": v(325, -635) * mm});
            skPoint(sketch, "E34.3.25.0", {"position": v(300, -635) * mm});
            skPoint(sketch, "E34.0.26.0", {"position": v(350, -660) * mm});
            skPoint(sketch, "E34.1.26.0", {"position": v(275, -660) * mm});
            skPoint(sketch, "E34.2.26.0", {"position": v(325, -660) * mm});
            skPoint(sketch, "E34.3.26.0", {"position": v(300, -660) * mm});
            skPoint(sketch, "E34.0.27.0", {"position": v(350, -685) * mm});
            skPoint(sketch, "E34.1.27.0", {"position": v(275, -685) * mm});
            skPoint(sketch, "E34.2.27.0", {"position": v(325, -685) * mm});
            skPoint(sketch, "E34.3.27.0", {"position": v(300, -685) * mm});
            skPoint(sketch, "E34.0.28.0", {"position": v(350, -710) * mm});
            skPoint(sketch, "E34.1.28.0", {"position": v(275, -710) * mm});
            skPoint(sketch, "E34.2.28.0", {"position": v(325, -710) * mm});
            skPoint(sketch, "E34.3.28.0", {"position": v(300, -710) * mm});
            skPoint(sketch, "E34.0.29.0", {"position": v(350, -735) * mm});
            skPoint(sketch, "E34.1.29.0", {"position": v(275, -735) * mm});
            skPoint(sketch, "E34.2.29.0", {"position": v(325, -735) * mm});
            skPoint(sketch, "E34.3.29.0", {"position": v(300, -735) * mm});
            skPoint(sketch, "E34.0.30.0", {"position": v(350, -760) * mm});
            skPoint(sketch, "E34.1.30.0", {"position": v(275, -760) * mm});
            skPoint(sketch, "E34.2.30.0", {"position": v(325, -760) * mm});
            skPoint(sketch, "E34.3.30.0", {"position": v(300, -760) * mm});
            skPoint(sketch, "E34.0.31.0", {"position": v(350, -785) * mm});
            skPoint(sketch, "E34.1.31.0", {"position": v(275, -785) * mm});
            skPoint(sketch, "E34.2.31.0", {"position": v(325, -785) * mm});
            skPoint(sketch, "E34.3.31.0", {"position": v(300, -785) * mm});
            skPoint(sketch, "E34.0.32.0", {"position": v(350, -810) * mm});
            skPoint(sketch, "E34.1.32.0", {"position": v(275, -810) * mm});
            skPoint(sketch, "E34.2.32.0", {"position": v(325, -810) * mm});
            skPoint(sketch, "E34.3.32.0", {"position": v(300, -810) * mm});
            skPoint(sketch, "E34.0.33.0", {"position": v(350, -835) * mm});
            skPoint(sketch, "E34.1.33.0", {"position": v(275, -835) * mm});
            skPoint(sketch, "E34.2.33.0", {"position": v(325, -835) * mm});
            skPoint(sketch, "E34.3.33.0", {"position": v(300, -835) * mm});
            skPoint(sketch, "E34.0.34.0", {"position": v(350, -860) * mm});
            skPoint(sketch, "E34.1.34.0", {"position": v(275, -860) * mm});
            skPoint(sketch, "E34.2.34.0", {"position": v(325, -860) * mm});
            skPoint(sketch, "E34.3.34.0", {"position": v(300, -860) * mm});
            skPoint(sketch, "E34.0.35.0", {"position": v(350, -885) * mm});
            skPoint(sketch, "E34.1.35.0", {"position": v(275, -885) * mm});
            skPoint(sketch, "E34.2.35.0", {"position": v(325, -885) * mm});
            skPoint(sketch, "E34.3.35.0", {"position": v(300, -885) * mm});
            skPoint(sketch, "E34.0.36.0", {"position": v(350, -910) * mm});
            skPoint(sketch, "E34.1.36.0", {"position": v(275, -910) * mm});
            skPoint(sketch, "E34.2.36.0", {"position": v(325, -910) * mm});
            skPoint(sketch, "E34.3.36.0", {"position": v(300, -910) * mm});
            skPoint(sketch, "E34.0.37.0", {"position": v(350, -935) * mm});
            skPoint(sketch, "E34.1.37.0", {"position": v(275, -935) * mm});
            skPoint(sketch, "E34.2.37.0", {"position": v(325, -935) * mm});
            skPoint(sketch, "E34.3.37.0", {"position": v(300, -935) * mm});
            skPoint(sketch, "E34.0.38.0", {"position": v(350, -960) * mm});
            skPoint(sketch, "E34.1.38.0", {"position": v(275, -960) * mm});
            skPoint(sketch, "E34.2.38.0", {"position": v(325, -960) * mm});
            skPoint(sketch, "E34.3.38.0", {"position": v(300, -960) * mm});
            skPoint(sketch, "E34.0.39.0", {"position": v(350, -985) * mm});
            skPoint(sketch, "E34.1.39.0", {"position": v(275, -985) * mm});
            skPoint(sketch, "E34.2.39.0", {"position": v(325, -985) * mm});
            skPoint(sketch, "E34.3.39.0", {"position": v(300, -985) * mm});
            skPoint(sketch, "E34.0.40.0", {"position": v(350, -1010) * mm});
            skPoint(sketch, "E34.1.40.0", {"position": v(275, -1010) * mm});
            skPoint(sketch, "E34.2.40.0", {"position": v(325, -1010) * mm});
            skPoint(sketch, "E34.3.40.0", {"position": v(300, -1010) * mm});
            skPoint(sketch, "E34.0.41.0", {"position": v(350, -1035) * mm});
            skPoint(sketch, "E34.1.41.0", {"position": v(275, -1035) * mm});
            skPoint(sketch, "E34.2.41.0", {"position": v(325, -1035) * mm});
            skPoint(sketch, "E34.3.41.0", {"position": v(300, -1035) * mm});
            skPoint(sketch, "E34.0.42.0", {"position": v(350, -1060) * mm});
            skPoint(sketch, "E34.1.42.0", {"position": v(275, -1060) * mm});
            skPoint(sketch, "E34.2.42.0", {"position": v(325, -1060) * mm});
            skPoint(sketch, "E34.3.42.0", {"position": v(300, -1060) * mm});
            skPoint(sketch, "E34.0.43.0", {"position": v(350, -1085) * mm});
            skPoint(sketch, "E34.1.43.0", {"position": v(275, -1085) * mm});
            skPoint(sketch, "E34.2.43.0", {"position": v(325, -1085) * mm});
            skPoint(sketch, "E34.3.43.0", {"position": v(300, -1085) * mm});
            skPoint(sketch, "E34.0.44.0", {"position": v(350, -1110) * mm});
            skPoint(sketch, "E34.1.44.0", {"position": v(275, -1110) * mm});
            skPoint(sketch, "E34.2.44.0", {"position": v(325, -1110) * mm});
            skPoint(sketch, "E34.3.44.0", {"position": v(300, -1110) * mm});
            skPoint(sketch, "E34.0.45.0", {"position": v(350, -1135) * mm});
            skPoint(sketch, "E34.1.45.0", {"position": v(275, -1135) * mm});
            skPoint(sketch, "E34.2.45.0", {"position": v(325, -1135) * mm});
            skPoint(sketch, "E34.3.45.0", {"position": v(300, -1135) * mm});
            skPoint(sketch, "E34.0.46.0", {"position": v(350, -1160) * mm});
            skPoint(sketch, "E34.1.46.0", {"position": v(275, -1160) * mm});
            skPoint(sketch, "E34.2.46.0", {"position": v(325, -1160) * mm});
            skPoint(sketch, "E34.3.46.0", {"position": v(300, -1160) * mm});
            skPoint(sketch, "E34.0.47.0", {"position": v(350, -1185) * mm});
            skPoint(sketch, "E34.1.47.0", {"position": v(275, -1185) * mm});
            skPoint(sketch, "E34.2.47.0", {"position": v(325, -1185) * mm});
            skPoint(sketch, "E34.3.47.0", {"position": v(300, -1185) * mm});
            skPoint(sketch, "E34.0.48.0", {"position": v(350, -1210) * mm});
            skPoint(sketch, "E34.1.48.0", {"position": v(275, -1210) * mm});
            skPoint(sketch, "E34.2.48.0", {"position": v(325, -1210) * mm});
            skPoint(sketch, "E34.3.48.0", {"position": v(300, -1210) * mm});
            skPoint(sketch, "E34.0.49.0", {"position": v(350, -1235) * mm});
            skPoint(sketch, "E34.1.49.0", {"position": v(275, -1235) * mm});
            skPoint(sketch, "E34.2.49.0", {"position": v(325, -1235) * mm});
            skPoint(sketch, "E34.3.49.0", {"position": v(300, -1235) * mm});
            skPoint(sketch, "E34.0.50.0", {"position": v(350, -1260) * mm});
            skPoint(sketch, "E34.1.50.0", {"position": v(275, -1260) * mm});
            skPoint(sketch, "E34.2.50.0", {"position": v(325, -1260) * mm});
            skPoint(sketch, "E34.3.50.0", {"position": v(300, -1260) * mm});
            skPoint(sketch, "E34.0.51.0", {"position": v(350, -1285) * mm});
            skPoint(sketch, "E34.1.51.0", {"position": v(275, -1285) * mm});
            skPoint(sketch, "E34.2.51.0", {"position": v(325, -1285) * mm});
            skPoint(sketch, "E34.3.51.0", {"position": v(300, -1285) * mm});
            skPoint(sketch, "E34.0.52.0", {"position": v(350, -1310) * mm});
            skPoint(sketch, "E34.1.52.0", {"position": v(275, -1310) * mm});
            skPoint(sketch, "E34.2.52.0", {"position": v(325, -1310) * mm});
            skPoint(sketch, "E34.3.52.0", {"position": v(300, -1310) * mm});
            skPoint(sketch, "E34.0.53.0", {"position": v(350, -1335) * mm});
            skPoint(sketch, "E34.1.53.0", {"position": v(275, -1335) * mm});
            skPoint(sketch, "E34.2.53.0", {"position": v(325, -1335) * mm});
            skPoint(sketch, "E34.3.53.0", {"position": v(300, -1335) * mm});
            skPoint(sketch, "E34.0.54.0", {"position": v(350, -1360) * mm});
            skPoint(sketch, "E34.1.54.0", {"position": v(275, -1360) * mm});
            skPoint(sketch, "E34.2.54.0", {"position": v(325, -1360) * mm});
            skPoint(sketch, "E34.3.54.0", {"position": v(300, -1360) * mm});
            skPoint(sketch, "E34.0.55.0", {"position": v(350, -1385) * mm});
            skPoint(sketch, "E34.1.55.0", {"position": v(275, -1385) * mm});
            skPoint(sketch, "E34.2.55.0", {"position": v(325, -1385) * mm});
            skPoint(sketch, "E34.3.55.0", {"position": v(300, -1385) * mm});
            skPoint(sketch, "E34.0.56.0", {"position": v(350, -1410) * mm});
            skPoint(sketch, "E34.1.56.0", {"position": v(275, -1410) * mm});
            skPoint(sketch, "E34.2.56.0", {"position": v(325, -1410) * mm});
            skPoint(sketch, "E34.3.56.0", {"position": v(300, -1410) * mm});
            skPoint(sketch, "E34.0.57.0", {"position": v(350, -1435) * mm});
            skPoint(sketch, "E34.1.57.0", {"position": v(275, -1435) * mm});
            skPoint(sketch, "E34.2.57.0", {"position": v(325, -1435) * mm});
            skPoint(sketch, "E34.3.57.0", {"position": v(300, -1435) * mm});
            skPoint(sketch, "E34.0.58.0", {"position": v(350, -1460) * mm});
            skPoint(sketch, "E34.1.58.0", {"position": v(275, -1460) * mm});
            skPoint(sketch, "E34.2.58.0", {"position": v(325, -1460) * mm});
            skPoint(sketch, "E34.3.58.0", {"position": v(300, -1460) * mm});
            skPoint(sketch, "E34.0.59.0", {"position": v(350, -1485) * mm});
            skPoint(sketch, "E34.1.59.0", {"position": v(275, -1485) * mm});
            skPoint(sketch, "E34.2.59.0", {"position": v(325, -1485) * mm});
            skPoint(sketch, "E34.3.59.0", {"position": v(300, -1485) * mm});
            skPoint(sketch, "E34.0.60.0", {"position": v(350, -1510) * mm});
            skPoint(sketch, "E34.1.60.0", {"position": v(275, -1510) * mm});
            skPoint(sketch, "E34.2.60.0", {"position": v(325, -1510) * mm});
            skPoint(sketch, "E34.3.60.0", {"position": v(300, -1510) * mm});
            skPoint(sketch, "E34.0.61.0", {"position": v(350, -1535) * mm});
            skPoint(sketch, "E34.1.61.0", {"position": v(275, -1535) * mm});
            skPoint(sketch, "E34.2.61.0", {"position": v(325, -1535) * mm});
            skPoint(sketch, "E34.3.61.0", {"position": v(300, -1535) * mm});
            skPoint(sketch, "E34.0.62.0", {"position": v(350, -1560) * mm});
            skPoint(sketch, "E34.1.62.0", {"position": v(275, -1560) * mm});
            skPoint(sketch, "E34.2.62.0", {"position": v(325, -1560) * mm});
            skPoint(sketch, "E34.3.62.0", {"position": v(300, -1560) * mm});
            skPoint(sketch, "E34.0.63.0", {"position": v(350, -1585) * mm});
            skPoint(sketch, "E34.1.63.0", {"position": v(275, -1585) * mm});
            skPoint(sketch, "E34.2.63.0", {"position": v(325, -1585) * mm});
            skPoint(sketch, "E34.3.63.0", {"position": v(300, -1585) * mm});
            skPoint(sketch, "E34.0.64.0", {"position": v(350, -1610) * mm});
            skPoint(sketch, "E34.1.64.0", {"position": v(275, -1610) * mm});
            skPoint(sketch, "E34.2.64.0", {"position": v(325, -1610) * mm});
            skPoint(sketch, "E34.3.64.0", {"position": v(300, -1610) * mm});
            skPoint(sketch, "E34.0.65.0", {"position": v(350, -1635) * mm});
            skPoint(sketch, "E34.1.65.0", {"position": v(275, -1635) * mm});
            skPoint(sketch, "E34.2.65.0", {"position": v(325, -1635) * mm});
            skPoint(sketch, "E34.3.65.0", {"position": v(300, -1635) * mm});
            skPoint(sketch, "E34.0.66.0", {"position": v(350, -1660) * mm});
            skPoint(sketch, "E34.1.66.0", {"position": v(275, -1660) * mm});
            skPoint(sketch, "E34.2.66.0", {"position": v(325, -1660) * mm});
            skPoint(sketch, "E34.3.66.0", {"position": v(300, -1660) * mm});
            skPoint(sketch, "E34.0.67.0", {"position": v(350, -1685) * mm});
            skPoint(sketch, "E34.1.67.0", {"position": v(275, -1685) * mm});
            skPoint(sketch, "E34.2.67.0", {"position": v(325, -1685) * mm});
            skPoint(sketch, "E34.3.67.0", {"position": v(300, -1685) * mm});
            skPoint(sketch, "E34.0.68.0", {"position": v(350, -1710) * mm});
            skPoint(sketch, "E34.1.68.0", {"position": v(275, -1710) * mm});
            skPoint(sketch, "E34.2.68.0", {"position": v(325, -1710) * mm});
            skPoint(sketch, "E34.3.68.0", {"position": v(300, -1710) * mm});
            skPoint(sketch, "E34.0.69.0", {"position": v(350, -1735) * mm});
            skPoint(sketch, "E34.1.69.0", {"position": v(275, -1735) * mm});
            skPoint(sketch, "E34.2.69.0", {"position": v(325, -1735) * mm});
            skPoint(sketch, "E34.3.69.0", {"position": v(300, -1735) * mm});
            skPoint(sketch, "E34.0.70.0", {"position": v(350, -1760) * mm});
            skPoint(sketch, "E34.1.70.0", {"position": v(275, -1760) * mm});
            skPoint(sketch, "E34.2.70.0", {"position": v(325, -1760) * mm});
            skPoint(sketch, "E34.3.70.0", {"position": v(300, -1760) * mm});
            skPoint(sketch, "E34.0.71.0", {"position": v(350, -1785) * mm});
            skPoint(sketch, "E34.1.71.0", {"position": v(275, -1785) * mm});
            skPoint(sketch, "E34.2.71.0", {"position": v(325, -1785) * mm});
            skPoint(sketch, "E34.3.71.0", {"position": v(300, -1785) * mm});
            skPoint(sketch, "E34.0.72.0", {"position": v(350, -1810) * mm});
            skPoint(sketch, "E34.1.72.0", {"position": v(275, -1810) * mm});
            skPoint(sketch, "E34.2.72.0", {"position": v(325, -1810) * mm});
            skPoint(sketch, "E34.3.72.0", {"position": v(300, -1810) * mm});
            skPoint(sketch, "E34.0.73.0", {"position": v(350, -1835) * mm});
            skPoint(sketch, "E34.1.73.0", {"position": v(275, -1835) * mm});
            skPoint(sketch, "E34.2.73.0", {"position": v(325, -1835) * mm});
            skPoint(sketch, "E34.3.73.0", {"position": v(300, -1835) * mm});
            skPoint(sketch, "E34.0.74.0", {"position": v(350, -1860) * mm});
            skPoint(sketch, "E34.1.74.0", {"position": v(275, -1860) * mm});
            skPoint(sketch, "E34.2.74.0", {"position": v(325, -1860) * mm});
            skPoint(sketch, "E34.3.74.0", {"position": v(300, -1860) * mm});
            skPoint(sketch, "E34.0.75.0", {"position": v(350, -1885) * mm});
            skPoint(sketch, "E34.1.75.0", {"position": v(275, -1885) * mm});
            skPoint(sketch, "E34.2.75.0", {"position": v(325, -1885) * mm});
            skPoint(sketch, "E34.3.75.0", {"position": v(300, -1885) * mm});
            skPoint(sketch, "E34.0.76.0", {"position": v(350, -1910) * mm});
            skPoint(sketch, "E34.1.76.0", {"position": v(275, -1910) * mm});
            skPoint(sketch, "E34.2.76.0", {"position": v(325, -1910) * mm});
            skPoint(sketch, "E34.3.76.0", {"position": v(300, -1910) * mm});
            skPoint(sketch, "E34.0.77.0", {"position": v(350, -1935) * mm});
            skPoint(sketch, "E34.1.77.0", {"position": v(275, -1935) * mm});
            skPoint(sketch, "E34.2.77.0", {"position": v(325, -1935) * mm});
            skPoint(sketch, "E34.3.77.0", {"position": v(300, -1935) * mm});
            skPoint(sketch, "E34.0.78.0", {"position": v(350, -1960) * mm});
            skPoint(sketch, "E34.1.78.0", {"position": v(275, -1960) * mm});
            skPoint(sketch, "E34.2.78.0", {"position": v(325, -1960) * mm});
            skPoint(sketch, "E34.3.78.0", {"position": v(300, -1960) * mm});
            skPoint(sketch, "E34.0.79.0", {"position": v(350, -1985) * mm});
            skPoint(sketch, "E34.1.79.0", {"position": v(275, -1985) * mm});
            skPoint(sketch, "E34.2.79.0", {"position": v(325, -1985) * mm});
            skPoint(sketch, "E34.3.79.0", {"position": v(300, -1985) * mm});
            skSolve(sketch);
        }
        {
            var Q0;
            Q0=sQuery(id+"F16.wireOp",VERTEX,"E27.6.0.0");
            var Q1;
            Q1=sQuery(id+"F16.wireOp",VERTEX,"E30.1.0.1");
            var Q2;
            Q2=sQuery(id+"F16.wireOp",VERTEX,"E29.0.9.0");
            var Q3;
            Q3=sQuery(id+"F16.wireOp",VERTEX,"E30.2.0.1");
            var Q4;
            Q4=sQuery(id+"F16.wireOp",VERTEX,"E28.2.0.2");
            var Q5;
            Q5=sQuery(id+"F16.wireOp",VERTEX,"E27.1.0.0");
            var Q6;
            Q6=sQuery(id+"F16.wireOp",VERTEX,"E28.2.0.5");
            var Q7;
            Q7=sQuery(id+"F16.wireOp",VERTEX,"E29.0.8.0");
            var Q8;
            Q8=sQuery(id+"F16.wireOp",VERTEX,"E27.3.0.0");
            var Q9;
            Q9=sQuery(id+"F16.wireOp",VERTEX,"E30.1.0.3");
            var Q10;
            Q10=sQuery(id+"F16.wireOp",VERTEX,"E28.2.0.1");
            var Q11;
            Q11=sQuery(id+"F16.wireOp",VERTEX,"E28.1.0.0");
            var Q12;
            Q12=sQuery(id+"F16.wireOp",VERTEX,"E29.0.7.0");
            var Q13;
            Q13=sQuery(id+"F16.wireOp",VERTEX,"E30.1.0.2");
            var Q14;
            Q14=sQuery(id+"F16.wireOp",VERTEX,"E30.2.0.2");
            var Q15;
            Q15=sQuery(id+"F16.wireOp",VERTEX,"E28.2.0.3");
            var Q16;
            Q16=sQuery(id+"F16.wireOp",VERTEX,"E28.2.0.6");
            var Q17;
            Q17=sQuery(id+"F16.wireOp",VERTEX,"E28.1.0.2");
            var Q18;
            Q18=sQuery(id+"F16.wireOp",VERTEX,"E27.4.0.0");
            var Q19;
            Q19=sQuery(id+"F16.wireOp",VERTEX,"E28.1.0.6");
            var Q20;
            Q20=sQuery(id+"F16.wireOp",VERTEX,"E28.1.0.1");
            var Q21;
            Q21=sQuery(id+"F16.wireOp",VERTEX,"E30.2.0.3");
            var Q22;
            Q22=sQuery(id+"F16.wireOp",VERTEX,"E26");
            var Q23;
            Q23=sQuery(id+"F16.wireOp",VERTEX,"E28.1.0.5");
            var Q24;
            Q24=sQuery(id+"F16.wireOp",VERTEX,"E27.2.0.0");
            var Q25;
            Q25=sQuery(id+"F16.wireOp",VERTEX,"E27.5.0.0");
            var Q26;
            Q26=sQuery(id+"F16.wireOp",VERTEX,"E28.1.0.4");
            var Q27;
            Q27=sQuery(id+"F16.wireOp",VERTEX,"E28.1.0.3");
            var Q28;
            Q28=sQuery(id+"F16.wireOp",VERTEX,"E28.2.0.0");
            var Q29;
            Q29=sQuery(id+"F16.wireOp",VERTEX,"E28.2.0.4");
            var Q30;
            Q30=sQuery(id+"F16.wireOp",VERTEX,"E28.3.0.6");
            var Q31;
            Q31=sQuery(id+"F16.wireOp",VERTEX,"E28.3.0.4");
            var Q32;
            Q32=sQuery(id+"F16.wireOp",VERTEX,"E31.1.3.0");
            var Q33;
            Q33=sQuery(id+"F16.wireOp",VERTEX,"E31.3.3.0");
            var Q34;
            Q34=sQuery(id+"F16.wireOp",VERTEX,"E28.3.0.3");
            var Q35;
            Q35=sQuery(id+"F16.wireOp",VERTEX,"E28.3.0.5");
            var Q36;
            Q36=sQuery(id+"F16.wireOp",VERTEX,"E28.3.0.1");
            var Q37;
            Q37=sQuery(id+"F16.wireOp",VERTEX,"E31.2.3.0");
            var Q38;
            Q38=sQuery(id+"F16.wireOp",VERTEX,"E28.3.0.2");
            var Q39;
            Q39=sQuery(id+"F16.wireOp",VERTEX,"E28.4.0.2");
            var Q40;
            Q40=sQuery(id+"F16.wireOp",VERTEX,"E31.1.4.0");
            var Q41;
            Q41=sQuery(id+"F16.wireOp",VERTEX,"E31.1.5.0");
            var Q42;
            Q42=sQuery(id+"F16.wireOp",VERTEX,"E31.2.4.0");
            var Q43;
            Q43=sQuery(id+"F16.wireOp",VERTEX,"E28.4.0.5");
            var Q44;
            Q44=sQuery(id+"F16.wireOp",VERTEX,"E28.4.0.3");
            var Q45;
            Q45=sQuery(id+"F16.wireOp",VERTEX,"E28.5.0.4");
            var Q46;
            Q46=sQuery(id+"F16.wireOp",VERTEX,"E28.5.0.6");
            var Q47;
            Q47=sQuery(id+"F16.wireOp",VERTEX,"E28.5.0.5");
            var Q48;
            Q48=sQuery(id+"F16.wireOp",VERTEX,"E31.3.5.0");
            var Q49;
            Q49=sQuery(id+"F16.wireOp",VERTEX,"E28.4.0.4");
            var Q50;
            Q50=sQuery(id+"F16.wireOp",VERTEX,"E31.2.5.0");
            var Q51;
            Q51=sQuery(id+"F16.wireOp",VERTEX,"E28.5.0.3");
            var Q52;
            Q52=sQuery(id+"F16.wireOp",VERTEX,"E31.3.4.0");
            var Q53;
            Q53=sQuery(id+"F16.wireOp",VERTEX,"E28.4.0.6");
            var Q54;
            Q54=sQuery(id+"F16.wireOp",VERTEX,"E31.2.6.0");
            var Q55;
            Q55=sQuery(id+"F16.wireOp",VERTEX,"E28.6.0.6");
            var Q56;
            Q56=sQuery(id+"F16.wireOp",VERTEX,"E28.6.0.5");
            var Q57;
            Q57=sQuery(id+"F16.wireOp",VERTEX,"E31.3.6.0");
            var Q58;
            Q58=sQuery(id+"F16.wireOp",VERTEX,"E28.6.0.4");
            var Q59;
            Q59=sQuery(id+"F16.wireOp",VERTEX,"E31.1.6.0");
            var Q60;
            Q60=sQuery(id+"F16.wireOp",VERTEX,"E31.3.7.0");
            var Q61;
            Q61=sQuery(id+"F16.wireOp",VERTEX,"E31.2.7.0");
            var Q62;
            Q62=sQuery(id+"F16.wireOp",VERTEX,"E28.7.0.6");
            var Q63;
            Q63=sQuery(id+"F16.wireOp",VERTEX,"E28.7.0.5");
            var Q64;
            Q64=sQuery(id+"F16.wireOp",VERTEX,"E31.1.7.0");
            var Q65;
            Q65=sQuery(id+"F16.wireOp",VERTEX,"E31.2.10.0");
            var Q66;
            Q66=sQuery(id+"F16.wireOp",VERTEX,"E31.1.12.0");
            var Q67;
            Q67=sQuery(id+"F16.wireOp",VERTEX,"E31.1.10.0");
            var Q68;
            Q68=sQuery(id+"F16.wireOp",VERTEX,"E31.1.11.0");
            var Q69;
            Q69=sQuery(id+"F16.wireOp",VERTEX,"E28.8.0.6");
            var Q70;
            Q70=sQuery(id+"F16.wireOp",VERTEX,"E31.2.9.0");
            var Q71;
            Q71=sQuery(id+"F16.wireOp",VERTEX,"E31.1.8.0");
            var Q72;
            Q72=sQuery(id+"F16.wireOp",VERTEX,"E31.1.9.0");
            var Q73;
            Q73=sQuery(id+"F16.wireOp",VERTEX,"E31.2.8.0");
            var Q74;
            Q74=sQuery(id+"F16.wireOp",VERTEX,"E31.3.9.0");
            var Q75;
            Q75=sQuery(id+"F16.wireOp",VERTEX,"E31.3.8.0");
            var Q76;
            Q76=makeQuery(id+"F6.opExtrude","SWEPT_BODY",BODY,{"disambiguationData":[OSD([sQuery(id+"F0.wireOp",EDGE,"E23.5.0.1"),sQuery(id+"F0.wireOp",EDGE,"E23.5.0.2"),sQuery(id+"F0.wireOp",EDGE,"E23.5.0.3"),sQuery(id+"F0.wireOp",EDGE,"E23.5.0.4"),sQuery(id+"F0.wireOp",EDGE,"E23.5.0.11"),sQuery(id+"F0.wireOp",EDGE,"E23.5.0.12"),sQuery(id+"F0.wireOp",EDGE,"E23.5.0.13"),sQuery(id+"F0.wireOp",EDGE,"E23.5.0.14"),sQuery(id+"F0.wireOp",EDGE,"E23.5.0.15"),sQuery(id+"F0.wireOp",EDGE,"E23.5.0.16"),sQuery(id+"F0.wireOp",EDGE,"E23.5.0.18"),sQuery(id+"F0.wireOp",EDGE,"E23.5.0.19"),sQuery(id+"F0.wireOp",EDGE,"E23.5.0.20"),sQuery(id+"F0.wireOp",EDGE,"E23.5.0.21"),sQuery(id+"F0.wireOp",EDGE,"E23.5.0.22"),sQuery(id+"F0.wireOp",EDGE,"E23.5.0.23"),sQuery(id+"F0.wireOp",EDGE,"E23.5.0.24"),sQuery(id+"F0.wireOp",EDGE,"E23.5.0.25"),sQuery(id+"F0.wireOp",EDGE,"E23.5.0.26"),sQuery(id+"F0.wireOp",EDGE,"E23.5.0.27")])]});
            var Q77;
            Q77=makeQuery(id+"F10.opExtrude","SWEPT_BODY",BODY,{"disambiguationData":[OSD([sQuery(id+"F0.wireOp",EDGE,"E24.3.9.0"),sQuery(id+"F0.wireOp",EDGE,"E24.6.9.0"),sQuery(id+"F0.wireOp",EDGE,"E24.9.9.0"),sQuery(id+"F0.wireOp",EDGE,"E24.12.9.0"),sQuery(id+"F0.wireOp",EDGE,"E24.21.9.0"),sQuery(id+"F0.wireOp",EDGE,"E24.24.9.0"),sQuery(id+"F0.wireOp",EDGE,"E24.27.9.0"),sQuery(id+"F0.wireOp",EDGE,"E24.30.9.0"),sQuery(id+"F0.wireOp",EDGE,"E24.33.9.0"),sQuery(id+"F0.wireOp",EDGE,"E24.36.9.0"),sQuery(id+"F0.wireOp",EDGE,"E24.43.9.0"),sQuery(id+"F0.wireOp",EDGE,"E24.46.9.0"),sQuery(id+"F0.wireOp",EDGE,"E24.49.9.0"),sQuery(id+"F0.wireOp",EDGE,"E24.52.9.0"),sQuery(id+"F0.wireOp",EDGE,"E24.56.9.0"),sQuery(id+"F0.wireOp",EDGE,"E24.59.9.0"),sQuery(id+"F0.wireOp",EDGE,"E24.63.9.0"),sQuery(id+"F0.wireOp",EDGE,"E24.66.9.0"),sQuery(id+"F0.wireOp",EDGE,"E24.70.9.0"),sQuery(id+"F0.wireOp",EDGE,"E24.74.9.0")])]});
            var Q78;
            Q78=makeQuery(id+"F2.opExtrude","SWEPT_BODY",BODY,{"disambiguationData":[OSD([sQuery(id+"F0.wireOp",EDGE,"E23.1.0.1"),sQuery(id+"F0.wireOp",EDGE,"E23.1.0.2"),sQuery(id+"F0.wireOp",EDGE,"E23.1.0.3"),sQuery(id+"F0.wireOp",EDGE,"E23.1.0.4"),sQuery(id+"F0.wireOp",EDGE,"E23.1.0.11"),sQuery(id+"F0.wireOp",EDGE,"E23.1.0.12"),sQuery(id+"F0.wireOp",EDGE,"E23.1.0.13"),sQuery(id+"F0.wireOp",EDGE,"E23.1.0.14"),sQuery(id+"F0.wireOp",EDGE,"E23.1.0.15"),sQuery(id+"F0.wireOp",EDGE,"E23.1.0.16"),sQuery(id+"F0.wireOp",EDGE,"E23.1.0.18"),sQuery(id+"F0.wireOp",EDGE,"E23.1.0.19"),sQuery(id+"F0.wireOp",EDGE,"E23.1.0.20"),sQuery(id+"F0.wireOp",EDGE,"E23.1.0.21"),sQuery(id+"F0.wireOp",EDGE,"E23.1.0.22"),sQuery(id+"F0.wireOp",EDGE,"E23.1.0.23"),sQuery(id+"F0.wireOp",EDGE,"E23.1.0.24"),sQuery(id+"F0.wireOp",EDGE,"E23.1.0.25"),sQuery(id+"F0.wireOp",EDGE,"E23.1.0.26"),sQuery(id+"F0.wireOp",EDGE,"E23.1.0.27")])]});
            var Q79;
            Q79=makeQuery(id+"F5.opExtrude","SWEPT_BODY",BODY,{"disambiguationData":[OSD([sQuery(id+"F0.wireOp",EDGE,"E23.4.0.1"),sQuery(id+"F0.wireOp",EDGE,"E23.4.0.2"),sQuery(id+"F0.wireOp",EDGE,"E23.4.0.3"),sQuery(id+"F0.wireOp",EDGE,"E23.4.0.4"),sQuery(id+"F0.wireOp",EDGE,"E23.4.0.11"),sQuery(id+"F0.wireOp",EDGE,"E23.4.0.12"),sQuery(id+"F0.wireOp",EDGE,"E23.4.0.13"),sQuery(id+"F0.wireOp",EDGE,"E23.4.0.14"),sQuery(id+"F0.wireOp",EDGE,"E23.4.0.15"),sQuery(id+"F0.wireOp",EDGE,"E23.4.0.16"),sQuery(id+"F0.wireOp",EDGE,"E23.4.0.18"),sQuery(id+"F0.wireOp",EDGE,"E23.4.0.19"),sQuery(id+"F0.wireOp",EDGE,"E23.4.0.20"),sQuery(id+"F0.wireOp",EDGE,"E23.4.0.21"),sQuery(id+"F0.wireOp",EDGE,"E23.4.0.22"),sQuery(id+"F0.wireOp",EDGE,"E23.4.0.23"),sQuery(id+"F0.wireOp",EDGE,"E23.4.0.24"),sQuery(id+"F0.wireOp",EDGE,"E23.4.0.25"),sQuery(id+"F0.wireOp",EDGE,"E23.4.0.26"),sQuery(id+"F0.wireOp",EDGE,"E23.4.0.27")])]});
            var Q80;
            Q80=makeQuery(id+"F11.opExtrude","SWEPT_BODY",BODY,{"disambiguationData":[OSD([sQuery(id+"F0.wireOp",EDGE,"E24.3.10.0"),sQuery(id+"F0.wireOp",EDGE,"E24.6.10.0"),sQuery(id+"F0.wireOp",EDGE,"E24.9.10.0"),sQuery(id+"F0.wireOp",EDGE,"E24.12.10.0"),sQuery(id+"F0.wireOp",EDGE,"E24.21.10.0"),sQuery(id+"F0.wireOp",EDGE,"E24.24.10.0"),sQuery(id+"F0.wireOp",EDGE,"E24.27.10.0"),sQuery(id+"F0.wireOp",EDGE,"E24.30.10.0"),sQuery(id+"F0.wireOp",EDGE,"E24.33.10.0"),sQuery(id+"F0.wireOp",EDGE,"E24.36.10.0"),sQuery(id+"F0.wireOp",EDGE,"E24.43.10.0"),sQuery(id+"F0.wireOp",EDGE,"E24.46.10.0"),sQuery(id+"F0.wireOp",EDGE,"E24.49.10.0"),sQuery(id+"F0.wireOp",EDGE,"E24.52.10.0"),sQuery(id+"F0.wireOp",EDGE,"E24.56.10.0"),sQuery(id+"F0.wireOp",EDGE,"E24.59.10.0"),sQuery(id+"F0.wireOp",EDGE,"E24.63.10.0"),sQuery(id+"F0.wireOp",EDGE,"E24.66.10.0"),sQuery(id+"F0.wireOp",EDGE,"E24.70.10.0"),sQuery(id+"F0.wireOp",EDGE,"E24.74.10.0")])]});
            var Q81;
            Q81=makeQuery(id+"F7.opExtrude","SWEPT_BODY",BODY,{"disambiguationData":[OSD([sQuery(id+"F0.wireOp",EDGE,"E23.6.0.1"),sQuery(id+"F0.wireOp",EDGE,"E23.6.0.2"),sQuery(id+"F0.wireOp",EDGE,"E23.6.0.3"),sQuery(id+"F0.wireOp",EDGE,"E23.6.0.4"),sQuery(id+"F0.wireOp",EDGE,"E23.6.0.11"),sQuery(id+"F0.wireOp",EDGE,"E23.6.0.12"),sQuery(id+"F0.wireOp",EDGE,"E23.6.0.13"),sQuery(id+"F0.wireOp",EDGE,"E23.6.0.14"),sQuery(id+"F0.wireOp",EDGE,"E23.6.0.15"),sQuery(id+"F0.wireOp",EDGE,"E23.6.0.16"),sQuery(id+"F0.wireOp",EDGE,"E23.6.0.18"),sQuery(id+"F0.wireOp",EDGE,"E23.6.0.19"),sQuery(id+"F0.wireOp",EDGE,"E23.6.0.20"),sQuery(id+"F0.wireOp",EDGE,"E23.6.0.21"),sQuery(id+"F0.wireOp",EDGE,"E23.6.0.22"),sQuery(id+"F0.wireOp",EDGE,"E23.6.0.23"),sQuery(id+"F0.wireOp",EDGE,"E23.6.0.24"),sQuery(id+"F0.wireOp",EDGE,"E23.6.0.25"),sQuery(id+"F0.wireOp",EDGE,"E23.6.0.26"),sQuery(id+"F0.wireOp",EDGE,"E23.6.0.27")])]});
            var Q82;
            Q82=makeQuery(id+"F9.opExtrude","SWEPT_BODY",BODY,{"disambiguationData":[OSD([sQuery(id+"F0.wireOp",EDGE,"E24.3.8.0"),sQuery(id+"F0.wireOp",EDGE,"E24.6.8.0"),sQuery(id+"F0.wireOp",EDGE,"E24.9.8.0"),sQuery(id+"F0.wireOp",EDGE,"E24.12.8.0"),sQuery(id+"F0.wireOp",EDGE,"E24.21.8.0"),sQuery(id+"F0.wireOp",EDGE,"E24.24.8.0"),sQuery(id+"F0.wireOp",EDGE,"E24.27.8.0"),sQuery(id+"F0.wireOp",EDGE,"E24.30.8.0"),sQuery(id+"F0.wireOp",EDGE,"E24.33.8.0"),sQuery(id+"F0.wireOp",EDGE,"E24.36.8.0"),sQuery(id+"F0.wireOp",EDGE,"E24.43.8.0"),sQuery(id+"F0.wireOp",EDGE,"E24.46.8.0"),sQuery(id+"F0.wireOp",EDGE,"E24.49.8.0"),sQuery(id+"F0.wireOp",EDGE,"E24.52.8.0"),sQuery(id+"F0.wireOp",EDGE,"E24.56.8.0"),sQuery(id+"F0.wireOp",EDGE,"E24.59.8.0"),sQuery(id+"F0.wireOp",EDGE,"E24.63.8.0"),sQuery(id+"F0.wireOp",EDGE,"E24.66.8.0"),sQuery(id+"F0.wireOp",EDGE,"E24.70.8.0"),sQuery(id+"F0.wireOp",EDGE,"E24.74.8.0")])]});
            var Q83;
            Q83=makeQuery(id+"F3.opExtrude","SWEPT_BODY",BODY,{"disambiguationData":[OSD([sQuery(id+"F0.wireOp",EDGE,"E23.2.0.1"),sQuery(id+"F0.wireOp",EDGE,"E23.2.0.2"),sQuery(id+"F0.wireOp",EDGE,"E23.2.0.3"),sQuery(id+"F0.wireOp",EDGE,"E23.2.0.4"),sQuery(id+"F0.wireOp",EDGE,"E23.2.0.11"),sQuery(id+"F0.wireOp",EDGE,"E23.2.0.12"),sQuery(id+"F0.wireOp",EDGE,"E23.2.0.13"),sQuery(id+"F0.wireOp",EDGE,"E23.2.0.14"),sQuery(id+"F0.wireOp",EDGE,"E23.2.0.15"),sQuery(id+"F0.wireOp",EDGE,"E23.2.0.16"),sQuery(id+"F0.wireOp",EDGE,"E23.2.0.18"),sQuery(id+"F0.wireOp",EDGE,"E23.2.0.19"),sQuery(id+"F0.wireOp",EDGE,"E23.2.0.20"),sQuery(id+"F0.wireOp",EDGE,"E23.2.0.21"),sQuery(id+"F0.wireOp",EDGE,"E23.2.0.22"),sQuery(id+"F0.wireOp",EDGE,"E23.2.0.23"),sQuery(id+"F0.wireOp",EDGE,"E23.2.0.24"),sQuery(id+"F0.wireOp",EDGE,"E23.2.0.25"),sQuery(id+"F0.wireOp",EDGE,"E23.2.0.26"),sQuery(id+"F0.wireOp",EDGE,"E23.2.0.27")])]});
            var Q84;
            Q84=makeQuery(id+"F8.opExtrude","SWEPT_BODY",BODY,{"disambiguationData":[OSD([sQuery(id+"F0.wireOp",EDGE,"E24.3.7.0"),sQuery(id+"F0.wireOp",EDGE,"E24.6.7.0"),sQuery(id+"F0.wireOp",EDGE,"E24.9.7.0"),sQuery(id+"F0.wireOp",EDGE,"E24.12.7.0"),sQuery(id+"F0.wireOp",EDGE,"E24.21.7.0"),sQuery(id+"F0.wireOp",EDGE,"E24.24.7.0"),sQuery(id+"F0.wireOp",EDGE,"E24.27.7.0"),sQuery(id+"F0.wireOp",EDGE,"E24.30.7.0"),sQuery(id+"F0.wireOp",EDGE,"E24.33.7.0"),sQuery(id+"F0.wireOp",EDGE,"E24.36.7.0"),sQuery(id+"F0.wireOp",EDGE,"E24.43.7.0"),sQuery(id+"F0.wireOp",EDGE,"E24.46.7.0"),sQuery(id+"F0.wireOp",EDGE,"E24.49.7.0"),sQuery(id+"F0.wireOp",EDGE,"E24.52.7.0"),sQuery(id+"F0.wireOp",EDGE,"E24.56.7.0"),sQuery(id+"F0.wireOp",EDGE,"E24.59.7.0"),sQuery(id+"F0.wireOp",EDGE,"E24.63.7.0"),sQuery(id+"F0.wireOp",EDGE,"E24.66.7.0"),sQuery(id+"F0.wireOp",EDGE,"E24.70.7.0"),sQuery(id+"F0.wireOp",EDGE,"E24.74.7.0")])]});
            var Q85;
            Q85=makeQuery(id+"F1.opExtrude","SWEPT_BODY",BODY,{"disambiguationData":[OSD([sQuery(id+"F0.wireOp",EDGE,"E1.bottom"),sQuery(id+"F0.wireOp",EDGE,"E1.top"),sQuery(id+"F0.wireOp",EDGE,"E1.left"),sQuery(id+"F0.wireOp",EDGE,"E1.right"),sQuery(id+"F0.wireOp",EDGE,"E2"),sQuery(id+"F0.wireOp",EDGE,"E3"),sQuery(id+"F0.wireOp",EDGE,"E4"),sQuery(id+"F0.wireOp",EDGE,"E5"),sQuery(id+"F0.wireOp",EDGE,"E6"),sQuery(id+"F0.wireOp",EDGE,"E7"),sQuery(id+"F0.wireOp",EDGE,"E8"),sQuery(id+"F0.wireOp",EDGE,"E9.MirrorCS"),sQuery(id+"F0.wireOp",EDGE,"E10.MirrorCS"),sQuery(id+"F0.wireOp",EDGE,"E11.MirrorCS"),sQuery(id+"F0.wireOp",EDGE,"E13.trimOffspring"),sQuery(id+"F0.wireOp",EDGE,"E14.trimOffspring"),sQuery(id+"F0.wireOp",EDGE,"E16.trimOffspring"),sQuery(id+"F0.wireOp",EDGE,"E17.trimOffspring"),sQuery(id+"F0.wireOp",EDGE,"E20"),sQuery(id+"F0.wireOp",EDGE,"E21")])]});
            var Q86;
            Q86=makeQuery(id+"F4.opExtrude","SWEPT_BODY",BODY,{"disambiguationData":[OSD([sQuery(id+"F0.wireOp",EDGE,"E23.3.0.1"),sQuery(id+"F0.wireOp",EDGE,"E23.3.0.2"),sQuery(id+"F0.wireOp",EDGE,"E23.3.0.3"),sQuery(id+"F0.wireOp",EDGE,"E23.3.0.4"),sQuery(id+"F0.wireOp",EDGE,"E23.3.0.11"),sQuery(id+"F0.wireOp",EDGE,"E23.3.0.12"),sQuery(id+"F0.wireOp",EDGE,"E23.3.0.13"),sQuery(id+"F0.wireOp",EDGE,"E23.3.0.14"),sQuery(id+"F0.wireOp",EDGE,"E23.3.0.15"),sQuery(id+"F0.wireOp",EDGE,"E23.3.0.16"),sQuery(id+"F0.wireOp",EDGE,"E23.3.0.18"),sQuery(id+"F0.wireOp",EDGE,"E23.3.0.19"),sQuery(id+"F0.wireOp",EDGE,"E23.3.0.20"),sQuery(id+"F0.wireOp",EDGE,"E23.3.0.21"),sQuery(id+"F0.wireOp",EDGE,"E23.3.0.22"),sQuery(id+"F0.wireOp",EDGE,"E23.3.0.23"),sQuery(id+"F0.wireOp",EDGE,"E23.3.0.24"),sQuery(id+"F0.wireOp",EDGE,"E23.3.0.25"),sQuery(id+"F0.wireOp",EDGE,"E23.3.0.26"),sQuery(id+"F0.wireOp",EDGE,"E23.3.0.27")])]});
            hole(context, id + "F17", {"style" : HoleStyle.C_BORE, "endStyle" : HoleEndStyle.THROUGH, "holeDiameter" : 3.5 * mm, "cBoreDiameter" : 6 * mm, "cBoreDepth" : 4.5 * mm, "majorDiameter" : 5 * mm, "isTappedThrough" : true, "tappedDepth" : 12 * mm, "tapClearance" : 3, "locations" : qUnion([Q0, Q1, Q2, Q3, Q4, Q5, Q6, Q7, Q8, Q9, Q10, Q11, Q12, Q13, Q14, Q15, Q16, Q17, Q18, Q19, Q20, Q21, Q22, Q23, Q24, Q25, Q26, Q27, Q28, Q29, Q30, Q31, Q32, Q33, Q34, Q35, Q36, Q37, Q38, Q39, Q40, Q41, Q42, Q43, Q44, Q45, Q46, Q47, Q48, Q49, Q50, Q51, Q52, Q53, Q54, Q55, Q56, Q57, Q58, Q59, Q60, Q61, Q62, Q63, Q64, Q65, Q66, Q67, Q68, Q69, Q70, Q71, Q72, Q73, Q74, Q75]), "scope" : qUnion([Q76, Q77, Q78, Q79, Q80, Q81, Q82, Q83, Q84, Q85, Q86])});
        }
        {
            var Q0;
            Q0=sQuery(id+"F16.wireOp",VERTEX,"E31.0.3.0");
            var Q1;
            Q1=sQuery(id+"F16.wireOp",VERTEX,"E31.0.4.0");
            var Q2;
            Q2=sQuery(id+"F16.wireOp",VERTEX,"E31.0.8.0");
            var Q3;
            Q3=sQuery(id+"F16.wireOp",VERTEX,"E31.0.7.0");
            var Q4;
            Q4=sQuery(id+"F16.wireOp",VERTEX,"E31.0.10.0");
            var Q5;
            Q5=sQuery(id+"F16.wireOp",VERTEX,"E31.0.12.0");
            var Q6;
            Q6=sQuery(id+"F16.wireOp",VERTEX,"E31.0.5.0");
            var Q7;
            Q7=sQuery(id+"F16.wireOp",VERTEX,"E30.1.0.0");
            var Q8;
            Q8=sQuery(id+"F16.wireOp",VERTEX,"E31.0.11.0");
            var Q9;
            Q9=sQuery(id+"F16.wireOp",VERTEX,"E31.0.14.0");
            var Q10;
            Q10=sQuery(id+"F16.wireOp",VERTEX,"E30.2.0.0");
            var Q11;
            Q11=sQuery(id+"F16.wireOp",VERTEX,"E31.0.6.0");
            var Q12;
            Q12=sQuery(id+"F16.wireOp",VERTEX,"E29.0.10.0");
            var Q13;
            Q13=sQuery(id+"F16.wireOp",VERTEX,"E31.0.9.0");
            var Q14;
            Q14=sQuery(id+"F16.wireOp",VERTEX,"E31.0.13.0");
            var Q15;
            Q15=sQuery(id+"F16.wireOp",VERTEX,"E34.1.18.0");
            var Q16;
            Q16=sQuery(id+"F16.wireOp",VERTEX,"E33.2.0.1");
            var Q17;
            Q17=sQuery(id+"F16.wireOp",VERTEX,"E34.1.11.0");
            var Q18;
            Q18=sQuery(id+"F16.wireOp",VERTEX,"E32.0.11.0");
            var Q19;
            Q19=sQuery(id+"F16.wireOp",VERTEX,"E34.1.16.0");
            var Q20;
            Q20=sQuery(id+"F16.wireOp",VERTEX,"E34.1.8.0");
            var Q21;
            Q21=sQuery(id+"F16.wireOp",VERTEX,"E33.1.0.1");
            var Q22;
            Q22=sQuery(id+"F16.wireOp",VERTEX,"E34.1.17.0");
            var Q23;
            Q23=sQuery(id+"F16.wireOp",VERTEX,"E34.1.13.0");
            var Q24;
            Q24=sQuery(id+"F16.wireOp",VERTEX,"E34.1.9.0");
            var Q25;
            Q25=sQuery(id+"F16.wireOp",VERTEX,"E34.1.5.0");
            var Q26;
            Q26=sQuery(id+"F16.wireOp",VERTEX,"E34.1.12.0");
            var Q27;
            Q27=sQuery(id+"F16.wireOp",VERTEX,"E34.1.4.0");
            var Q28;
            Q28=sQuery(id+"F16.wireOp",VERTEX,"E34.1.15.0");
            var Q29;
            Q29=sQuery(id+"F16.wireOp",VERTEX,"E34.1.7.0");
            var Q30;
            Q30=sQuery(id+"F16.wireOp",VERTEX,"E34.1.6.0");
            var Q31;
            Q31=sQuery(id+"F16.wireOp",VERTEX,"E34.1.3.0");
            var Q32;
            Q32=sQuery(id+"F16.wireOp",VERTEX,"E34.1.14.0");
            var Q33;
            Q33=sQuery(id+"F16.wireOp",VERTEX,"E34.1.10.0");
            var Q34;
            Q34=sQuery(id+"F16.wireOp",VERTEX,"E34.3.16.0");
            var Q35;
            Q35=sQuery(id+"F16.wireOp",VERTEX,"E34.3.12.0");
            var Q36;
            Q36=sQuery(id+"F16.wireOp",VERTEX,"E34.3.21.0");
            var Q37;
            Q37=sQuery(id+"F16.wireOp",VERTEX,"E34.3.20.0");
            var Q38;
            Q38=sQuery(id+"F16.wireOp",VERTEX,"E34.3.9.0");
            var Q39;
            Q39=sQuery(id+"F16.wireOp",VERTEX,"E34.3.13.0");
            var Q40;
            Q40=sQuery(id+"F16.wireOp",VERTEX,"E34.3.10.0");
            var Q41;
            Q41=sQuery(id+"F16.wireOp",VERTEX,"E34.3.15.0");
            var Q42;
            Q42=sQuery(id+"F16.wireOp",VERTEX,"E34.3.4.0");
            var Q43;
            Q43=sQuery(id+"F16.wireOp",VERTEX,"E33.1.0.3");
            var Q44;
            Q44=sQuery(id+"F16.wireOp",VERTEX,"E34.3.8.0");
            var Q45;
            Q45=sQuery(id+"F16.wireOp",VERTEX,"E34.3.19.0");
            var Q46;
            Q46=sQuery(id+"F16.wireOp",VERTEX,"E34.3.3.0");
            var Q47;
            Q47=sQuery(id+"F16.wireOp",VERTEX,"E34.3.7.0");
            var Q48;
            Q48=sQuery(id+"F16.wireOp",VERTEX,"E34.3.18.0");
            var Q49;
            Q49=sQuery(id+"F16.wireOp",VERTEX,"E34.3.22.0");
            var Q50;
            Q50=sQuery(id+"F16.wireOp",VERTEX,"E33.2.0.3");
            var Q51;
            Q51=sQuery(id+"F16.wireOp",VERTEX,"E34.3.6.0");
            var Q52;
            Q52=sQuery(id+"F16.wireOp",VERTEX,"E34.3.17.0");
            var Q53;
            Q53=sQuery(id+"F16.wireOp",VERTEX,"E34.3.14.0");
            var Q54;
            Q54=sQuery(id+"F16.wireOp",VERTEX,"E32.0.12.0");
            var Q55;
            Q55=sQuery(id+"F16.wireOp",VERTEX,"E34.3.5.0");
            var Q56;
            Q56=sQuery(id+"F16.wireOp",VERTEX,"E34.3.11.0");
            var Q57;
            Q57=sQuery(id+"F16.wireOp",VERTEX,"E33.2.0.2");
            var Q58;
            Q58=sQuery(id+"F16.wireOp",VERTEX,"E34.2.25.0");
            var Q59;
            Q59=sQuery(id+"F16.wireOp",VERTEX,"E34.2.16.0");
            var Q60;
            Q60=sQuery(id+"F16.wireOp",VERTEX,"E34.2.21.0");
            var Q61;
            Q61=sQuery(id+"F16.wireOp",VERTEX,"E34.2.13.0");
            var Q62;
            Q62=sQuery(id+"F16.wireOp",VERTEX,"E34.2.10.0");
            var Q63;
            Q63=sQuery(id+"F16.wireOp",VERTEX,"E34.2.22.0");
            var Q64;
            Q64=sQuery(id+"F16.wireOp",VERTEX,"E34.2.15.0");
            var Q65;
            Q65=sQuery(id+"F16.wireOp",VERTEX,"E34.2.26.0");
            var Q66;
            Q66=sQuery(id+"F16.wireOp",VERTEX,"E34.2.4.0");
            var Q67;
            Q67=sQuery(id+"F16.wireOp",VERTEX,"E32.0.13.0");
            var Q68;
            Q68=sQuery(id+"F16.wireOp",VERTEX,"E34.2.17.0");
            var Q69;
            Q69=sQuery(id+"F16.wireOp",VERTEX,"E34.2.5.0");
            var Q70;
            Q70=sQuery(id+"F16.wireOp",VERTEX,"E34.2.6.0");
            var Q71;
            Q71=sQuery(id+"F16.wireOp",VERTEX,"E33.1.0.2");
            var Q72;
            Q72=sQuery(id+"F16.wireOp",VERTEX,"E34.2.7.0");
            var Q73;
            Q73=sQuery(id+"F16.wireOp",VERTEX,"E34.2.18.0");
            var Q74;
            Q74=sQuery(id+"F16.wireOp",VERTEX,"E34.2.20.0");
            var Q75;
            Q75=sQuery(id+"F16.wireOp",VERTEX,"E34.2.12.0");
            var Q76;
            Q76=sQuery(id+"F16.wireOp",VERTEX,"E34.2.11.0");
            var Q77;
            Q77=sQuery(id+"F16.wireOp",VERTEX,"E34.2.9.0");
            var Q78;
            Q78=sQuery(id+"F16.wireOp",VERTEX,"E34.2.23.0");
            var Q79;
            Q79=sQuery(id+"F16.wireOp",VERTEX,"E34.2.24.0");
            var Q80;
            Q80=sQuery(id+"F16.wireOp",VERTEX,"E34.2.14.0");
            var Q81;
            Q81=sQuery(id+"F16.wireOp",VERTEX,"E34.2.27.0");
            var Q82;
            Q82=sQuery(id+"F16.wireOp",VERTEX,"E34.2.3.0");
            var Q83;
            Q83=sQuery(id+"F16.wireOp",VERTEX,"E34.2.19.0");
            var Q84;
            Q84=sQuery(id+"F16.wireOp",VERTEX,"E34.2.8.0");
            var Q85;
            Q85=makeQuery(id+"F11.opExtrude","SWEPT_BODY",BODY,{"disambiguationData":[OSD([sQuery(id+"F0.wireOp",EDGE,"E24.3.10.0"),sQuery(id+"F0.wireOp",EDGE,"E24.6.10.0"),sQuery(id+"F0.wireOp",EDGE,"E24.9.10.0"),sQuery(id+"F0.wireOp",EDGE,"E24.12.10.0"),sQuery(id+"F0.wireOp",EDGE,"E24.21.10.0"),sQuery(id+"F0.wireOp",EDGE,"E24.24.10.0"),sQuery(id+"F0.wireOp",EDGE,"E24.27.10.0"),sQuery(id+"F0.wireOp",EDGE,"E24.30.10.0"),sQuery(id+"F0.wireOp",EDGE,"E24.33.10.0"),sQuery(id+"F0.wireOp",EDGE,"E24.36.10.0"),sQuery(id+"F0.wireOp",EDGE,"E24.43.10.0"),sQuery(id+"F0.wireOp",EDGE,"E24.46.10.0"),sQuery(id+"F0.wireOp",EDGE,"E24.49.10.0"),sQuery(id+"F0.wireOp",EDGE,"E24.52.10.0"),sQuery(id+"F0.wireOp",EDGE,"E24.56.10.0"),sQuery(id+"F0.wireOp",EDGE,"E24.59.10.0"),sQuery(id+"F0.wireOp",EDGE,"E24.63.10.0"),sQuery(id+"F0.wireOp",EDGE,"E24.66.10.0"),sQuery(id+"F0.wireOp",EDGE,"E24.70.10.0"),sQuery(id+"F0.wireOp",EDGE,"E24.74.10.0")])]});
            var Q86;
            Q86=makeQuery(id+"F12.opExtrude","SWEPT_BODY",BODY,{"disambiguationData":[OSD([sQuery(id+"F0.wireOp",EDGE,"E25.3.11.0"),sQuery(id+"F0.wireOp",EDGE,"E25.6.11.0"),sQuery(id+"F0.wireOp",EDGE,"E25.9.11.0"),sQuery(id+"F0.wireOp",EDGE,"E25.12.11.0"),sQuery(id+"F0.wireOp",EDGE,"E25.21.11.0"),sQuery(id+"F0.wireOp",EDGE,"E25.24.11.0"),sQuery(id+"F0.wireOp",EDGE,"E25.27.11.0"),sQuery(id+"F0.wireOp",EDGE,"E25.30.11.0"),sQuery(id+"F0.wireOp",EDGE,"E25.33.11.0"),sQuery(id+"F0.wireOp",EDGE,"E25.36.11.0"),sQuery(id+"F0.wireOp",EDGE,"E25.43.11.0"),sQuery(id+"F0.wireOp",EDGE,"E25.46.11.0"),sQuery(id+"F0.wireOp",EDGE,"E25.49.11.0"),sQuery(id+"F0.wireOp",EDGE,"E25.52.11.0"),sQuery(id+"F0.wireOp",EDGE,"E25.56.11.0"),sQuery(id+"F0.wireOp",EDGE,"E25.59.11.0"),sQuery(id+"F0.wireOp",EDGE,"E25.63.11.0"),sQuery(id+"F0.wireOp",EDGE,"E25.66.11.0"),sQuery(id+"F0.wireOp",EDGE,"E25.70.11.0"),sQuery(id+"F0.wireOp",EDGE,"E25.74.11.0")])]});
            var Q87;
            Q87=makeQuery(id+"F13.opExtrude","SWEPT_BODY",BODY,{"disambiguationData":[OSD([sQuery(id+"F0.wireOp",EDGE,"E25.3.12.0"),sQuery(id+"F0.wireOp",EDGE,"E25.6.12.0"),sQuery(id+"F0.wireOp",EDGE,"E25.9.12.0"),sQuery(id+"F0.wireOp",EDGE,"E25.12.12.0"),sQuery(id+"F0.wireOp",EDGE,"E25.21.12.0"),sQuery(id+"F0.wireOp",EDGE,"E25.24.12.0"),sQuery(id+"F0.wireOp",EDGE,"E25.27.12.0"),sQuery(id+"F0.wireOp",EDGE,"E25.30.12.0"),sQuery(id+"F0.wireOp",EDGE,"E25.33.12.0"),sQuery(id+"F0.wireOp",EDGE,"E25.36.12.0"),sQuery(id+"F0.wireOp",EDGE,"E25.43.12.0"),sQuery(id+"F0.wireOp",EDGE,"E25.46.12.0"),sQuery(id+"F0.wireOp",EDGE,"E25.49.12.0"),sQuery(id+"F0.wireOp",EDGE,"E25.52.12.0"),sQuery(id+"F0.wireOp",EDGE,"E25.56.12.0"),sQuery(id+"F0.wireOp",EDGE,"E25.59.12.0"),sQuery(id+"F0.wireOp",EDGE,"E25.63.12.0"),sQuery(id+"F0.wireOp",EDGE,"E25.66.12.0"),sQuery(id+"F0.wireOp",EDGE,"E25.70.12.0"),sQuery(id+"F0.wireOp",EDGE,"E25.74.12.0")])]});
            var Q88;
            Q88=makeQuery(id+"F14.opExtrude","SWEPT_BODY",BODY,{"disambiguationData":[OSD([sQuery(id+"F0.wireOp",EDGE,"E25.3.13.0"),sQuery(id+"F0.wireOp",EDGE,"E25.6.13.0"),sQuery(id+"F0.wireOp",EDGE,"E25.9.13.0"),sQuery(id+"F0.wireOp",EDGE,"E25.12.13.0"),sQuery(id+"F0.wireOp",EDGE,"E25.21.13.0"),sQuery(id+"F0.wireOp",EDGE,"E25.24.13.0"),sQuery(id+"F0.wireOp",EDGE,"E25.27.13.0"),sQuery(id+"F0.wireOp",EDGE,"E25.30.13.0"),sQuery(id+"F0.wireOp",EDGE,"E25.33.13.0"),sQuery(id+"F0.wireOp",EDGE,"E25.36.13.0"),sQuery(id+"F0.wireOp",EDGE,"E25.43.13.0"),sQuery(id+"F0.wireOp",EDGE,"E25.46.13.0"),sQuery(id+"F0.wireOp",EDGE,"E25.49.13.0"),sQuery(id+"F0.wireOp",EDGE,"E25.52.13.0"),sQuery(id+"F0.wireOp",EDGE,"E25.56.13.0"),sQuery(id+"F0.wireOp",EDGE,"E25.59.13.0"),sQuery(id+"F0.wireOp",EDGE,"E25.63.13.0"),sQuery(id+"F0.wireOp",EDGE,"E25.66.13.0"),sQuery(id+"F0.wireOp",EDGE,"E25.70.13.0"),sQuery(id+"F0.wireOp",EDGE,"E25.74.13.0")])]});
            hole(context, id + "F18", {"style" : HoleStyle.C_BORE, "endStyle" : HoleEndStyle.THROUGH, "holeDiameter" : 3.5 * mm, "cBoreDiameter" : 6 * mm, "cBoreDepth" : 4.5 * mm, "majorDiameter" : 5 * mm, "isTappedThrough" : true, "tappedDepth" : 12 * mm, "tapClearance" : 3, "locations" : qUnion([Q0, Q1, Q2, Q3, Q4, Q5, Q6, Q7, Q8, Q9, Q10, Q11, Q12, Q13, Q14, Q15, Q16, Q17, Q18, Q19, Q20, Q21, Q22, Q23, Q24, Q25, Q26, Q27, Q28, Q29, Q30, Q31, Q32, Q33, Q34, Q35, Q36, Q37, Q38, Q39, Q40, Q41, Q42, Q43, Q44, Q45, Q46, Q47, Q48, Q49, Q50, Q51, Q52, Q53, Q54, Q55, Q56, Q57, Q58, Q59, Q60, Q61, Q62, Q63, Q64, Q65, Q66, Q67, Q68, Q69, Q70, Q71, Q72, Q73, Q74, Q75, Q76, Q77, Q78, Q79, Q80, Q81, Q82, Q83, Q84]), "scope" : qUnion([Q85, Q86, Q87, Q88])});
        }
        {
            var Q0;
            Q0=sQuery(id+"F16.wireOp",VERTEX,"E34.0.12.0");
            var Q1;
            Q1=sQuery(id+"F16.wireOp",VERTEX,"E34.0.6.0");
            var Q2;
            Q2=sQuery(id+"F16.wireOp",VERTEX,"E34.0.4.0");
            var Q3;
            Q3=sQuery(id+"F16.wireOp",VERTEX,"E34.0.10.0");
            var Q4;
            Q4=sQuery(id+"F16.wireOp",VERTEX,"E34.0.13.0");
            var Q5;
            Q5=sQuery(id+"F16.wireOp",VERTEX,"E34.0.8.0");
            var Q6;
            Q6=sQuery(id+"F16.wireOp",VERTEX,"E34.0.18.0");
            var Q7;
            Q7=sQuery(id+"F16.wireOp",VERTEX,"E32.0.14.0");
            var Q8;
            Q8=sQuery(id+"F16.wireOp",VERTEX,"E34.0.25.0");
            var Q9;
            Q9=sQuery(id+"F16.wireOp",VERTEX,"E34.0.22.0");
            var Q10;
            Q10=sQuery(id+"F16.wireOp",VERTEX,"E34.0.9.0");
            var Q11;
            Q11=sQuery(id+"F16.wireOp",VERTEX,"E34.0.24.0");
            var Q12;
            Q12=sQuery(id+"F16.wireOp",VERTEX,"E34.0.17.0");
            var Q13;
            Q13=sQuery(id+"F16.wireOp",VERTEX,"E34.0.16.0");
            var Q14;
            Q14=sQuery(id+"F16.wireOp",VERTEX,"E34.0.29.0");
            var Q15;
            Q15=sQuery(id+"F16.wireOp",VERTEX,"E34.0.26.0");
            var Q16;
            Q16=sQuery(id+"F16.wireOp",VERTEX,"E34.0.14.0");
            var Q17;
            Q17=sQuery(id+"F16.wireOp",VERTEX,"E33.1.0.0");
            var Q18;
            Q18=sQuery(id+"F16.wireOp",VERTEX,"E34.0.5.0");
            var Q19;
            Q19=sQuery(id+"F16.wireOp",VERTEX,"E34.0.15.0");
            var Q20;
            Q20=sQuery(id+"F16.wireOp",VERTEX,"E34.0.19.0");
            var Q21;
            Q21=sQuery(id+"F16.wireOp",VERTEX,"E34.0.3.0");
            var Q22;
            Q22=sQuery(id+"F16.wireOp",VERTEX,"E34.0.7.0");
            var Q23;
            Q23=sQuery(id+"F16.wireOp",VERTEX,"E34.0.11.0");
            var Q24;
            Q24=sQuery(id+"F16.wireOp",VERTEX,"E34.0.21.0");
            var Q25;
            Q25=sQuery(id+"F16.wireOp",VERTEX,"E34.0.20.0");
            var Q26;
            Q26=sQuery(id+"F16.wireOp",VERTEX,"E34.0.27.0");
            var Q27;
            Q27=sQuery(id+"F16.wireOp",VERTEX,"E34.0.23.0");
            var Q28;
            Q28=sQuery(id+"F16.wireOp",VERTEX,"E33.2.0.0");
            var Q29;
            Q29=sQuery(id+"F16.wireOp",VERTEX,"E34.0.28.0");
            var Q30;
            Q30=sQuery(id+"F16.wireOp",VERTEX,"E34.0.53.0");
            var Q31;
            Q31=sQuery(id+"F16.wireOp",VERTEX,"E34.0.32.0");
            var Q32;
            Q32=sQuery(id+"F16.wireOp",VERTEX,"E34.0.36.0");
            var Q33;
            Q33=sQuery(id+"F16.wireOp",VERTEX,"E34.0.58.0");
            var Q34;
            Q34=sQuery(id+"F16.wireOp",VERTEX,"E34.0.54.0");
            var Q35;
            Q35=sQuery(id+"F16.wireOp",VERTEX,"E34.0.37.0");
            var Q36;
            Q36=sQuery(id+"F16.wireOp",VERTEX,"E34.0.57.0");
            var Q37;
            Q37=sQuery(id+"F16.wireOp",VERTEX,"E34.0.52.0");
            var Q38;
            Q38=sQuery(id+"F16.wireOp",VERTEX,"E34.0.30.0");
            var Q39;
            Q39=sQuery(id+"F16.wireOp",VERTEX,"E34.0.60.0");
            var Q40;
            Q40=sQuery(id+"F16.wireOp",VERTEX,"E34.0.40.0");
            var Q41;
            Q41=sQuery(id+"F16.wireOp",VERTEX,"E34.0.45.0");
            var Q42;
            Q42=sQuery(id+"F16.wireOp",VERTEX,"E34.0.44.0");
            var Q43;
            Q43=sQuery(id+"F16.wireOp",VERTEX,"E34.0.50.0");
            var Q44;
            Q44=sQuery(id+"F16.wireOp",VERTEX,"E34.0.49.0");
            var Q45;
            Q45=sQuery(id+"F16.wireOp",VERTEX,"E34.0.55.0");
            var Q46;
            Q46=sQuery(id+"F16.wireOp",VERTEX,"E34.0.38.0");
            var Q47;
            Q47=sQuery(id+"F16.wireOp",VERTEX,"E34.0.47.0");
            var Q48;
            Q48=sQuery(id+"F16.wireOp",VERTEX,"E34.0.63.0");
            var Q49;
            Q49=sQuery(id+"F16.wireOp",VERTEX,"E34.0.34.0");
            var Q50;
            Q50=sQuery(id+"F16.wireOp",VERTEX,"E34.0.56.0");
            var Q51;
            Q51=sQuery(id+"F16.wireOp",VERTEX,"E34.0.33.0");
            var Q52;
            Q52=sQuery(id+"F16.wireOp",VERTEX,"E34.0.46.0");
            var Q53;
            Q53=sQuery(id+"F16.wireOp",VERTEX,"E34.0.48.0");
            var Q54;
            Q54=sQuery(id+"F16.wireOp",VERTEX,"E34.0.61.0");
            var Q55;
            Q55=sQuery(id+"F16.wireOp",VERTEX,"E34.0.43.0");
            var Q56;
            Q56=sQuery(id+"F16.wireOp",VERTEX,"E34.0.42.0");
            var Q57;
            Q57=sQuery(id+"F16.wireOp",VERTEX,"E34.0.35.0");
            var Q58;
            Q58=sQuery(id+"F16.wireOp",VERTEX,"E34.0.59.0");
            var Q59;
            Q59=sQuery(id+"F16.wireOp",VERTEX,"E34.0.31.0");
            var Q60;
            Q60=sQuery(id+"F16.wireOp",VERTEX,"E34.0.51.0");
            var Q61;
            Q61=sQuery(id+"F16.wireOp",VERTEX,"E34.0.62.0");
            var Q62;
            Q62=sQuery(id+"F16.wireOp",VERTEX,"E34.0.41.0");
            var Q63;
            Q63=sQuery(id+"F16.wireOp",VERTEX,"E34.0.39.0");
            var Q64;
            Q64=sQuery(id+"F16.wireOp",VERTEX,"E34.0.64.0");
            var Q65;
            Q65=sQuery(id+"F16.wireOp",VERTEX,"E34.0.77.0");
            var Q66;
            Q66=sQuery(id+"F16.wireOp",VERTEX,"E34.0.68.0");
            var Q67;
            Q67=sQuery(id+"F16.wireOp",VERTEX,"E34.0.74.0");
            var Q68;
            Q68=sQuery(id+"F16.wireOp",VERTEX,"E34.0.66.0");
            var Q69;
            Q69=sQuery(id+"F16.wireOp",VERTEX,"E34.0.79.0");
            var Q70;
            Q70=sQuery(id+"F16.wireOp",VERTEX,"E34.0.65.0");
            var Q71;
            Q71=sQuery(id+"F16.wireOp",VERTEX,"E34.0.72.0");
            var Q72;
            Q72=sQuery(id+"F16.wireOp",VERTEX,"E34.0.78.0");
            var Q73;
            Q73=sQuery(id+"F16.wireOp",VERTEX,"E34.0.70.0");
            var Q74;
            Q74=sQuery(id+"F16.wireOp",VERTEX,"E34.0.76.0");
            var Q75;
            Q75=sQuery(id+"F16.wireOp",VERTEX,"E34.0.71.0");
            var Q76;
            Q76=sQuery(id+"F16.wireOp",VERTEX,"E34.0.69.0");
            var Q77;
            Q77=sQuery(id+"F16.wireOp",VERTEX,"E34.0.73.0");
            var Q78;
            Q78=sQuery(id+"F16.wireOp",VERTEX,"E34.0.75.0");
            var Q79;
            Q79=sQuery(id+"F16.wireOp",VERTEX,"E34.0.67.0");
            var Q80;
            Q80=makeQuery(id+"F15.opExtrude","SWEPT_BODY",BODY,{"disambiguationData":[OSD([sQuery(id+"F0.wireOp",EDGE,"E25.3.14.0"),sQuery(id+"F0.wireOp",EDGE,"E25.6.14.0"),sQuery(id+"F0.wireOp",EDGE,"E25.9.14.0"),sQuery(id+"F0.wireOp",EDGE,"E25.12.14.0"),sQuery(id+"F0.wireOp",EDGE,"E25.21.14.0"),sQuery(id+"F0.wireOp",EDGE,"E25.24.14.0"),sQuery(id+"F0.wireOp",EDGE,"E25.27.14.0"),sQuery(id+"F0.wireOp",EDGE,"E25.30.14.0"),sQuery(id+"F0.wireOp",EDGE,"E25.33.14.0"),sQuery(id+"F0.wireOp",EDGE,"E25.36.14.0"),sQuery(id+"F0.wireOp",EDGE,"E25.43.14.0"),sQuery(id+"F0.wireOp",EDGE,"E25.46.14.0"),sQuery(id+"F0.wireOp",EDGE,"E25.49.14.0"),sQuery(id+"F0.wireOp",EDGE,"E25.52.14.0"),sQuery(id+"F0.wireOp",EDGE,"E25.56.14.0"),sQuery(id+"F0.wireOp",EDGE,"E25.59.14.0"),sQuery(id+"F0.wireOp",EDGE,"E25.63.14.0"),sQuery(id+"F0.wireOp",EDGE,"E25.66.14.0"),sQuery(id+"F0.wireOp",EDGE,"E25.70.14.0"),sQuery(id+"F0.wireOp",EDGE,"E25.74.14.0")])]});
            hole(context, id + "F19", {"style" : HoleStyle.C_BORE, "endStyle" : HoleEndStyle.THROUGH, "holeDiameter" : 3.5 * mm, "cBoreDiameter" : 6 * mm, "cBoreDepth" : 4.5 * mm, "majorDiameter" : 5 * mm, "isTappedThrough" : true, "tappedDepth" : 12 * mm, "tapClearance" : 3, "locations" : qUnion([Q0, Q1, Q2, Q3, Q4, Q5, Q6, Q7, Q8, Q9, Q10, Q11, Q12, Q13, Q14, Q15, Q16, Q17, Q18, Q19, Q20, Q21, Q22, Q23, Q24, Q25, Q26, Q27, Q28, Q29, Q30, Q31, Q32, Q33, Q34, Q35, Q36, Q37, Q38, Q39, Q40, Q41, Q42, Q43, Q44, Q45, Q46, Q47, Q48, Q49, Q50, Q51, Q52, Q53, Q54, Q55, Q56, Q57, Q58, Q59, Q60, Q61, Q62, Q63, Q64, Q65, Q66, Q67, Q68, Q69, Q70, Q71, Q72, Q73, Q74, Q75, Q76, Q77, Q78, Q79]), "scope" : qUnion([Q80])});
        }
    });
